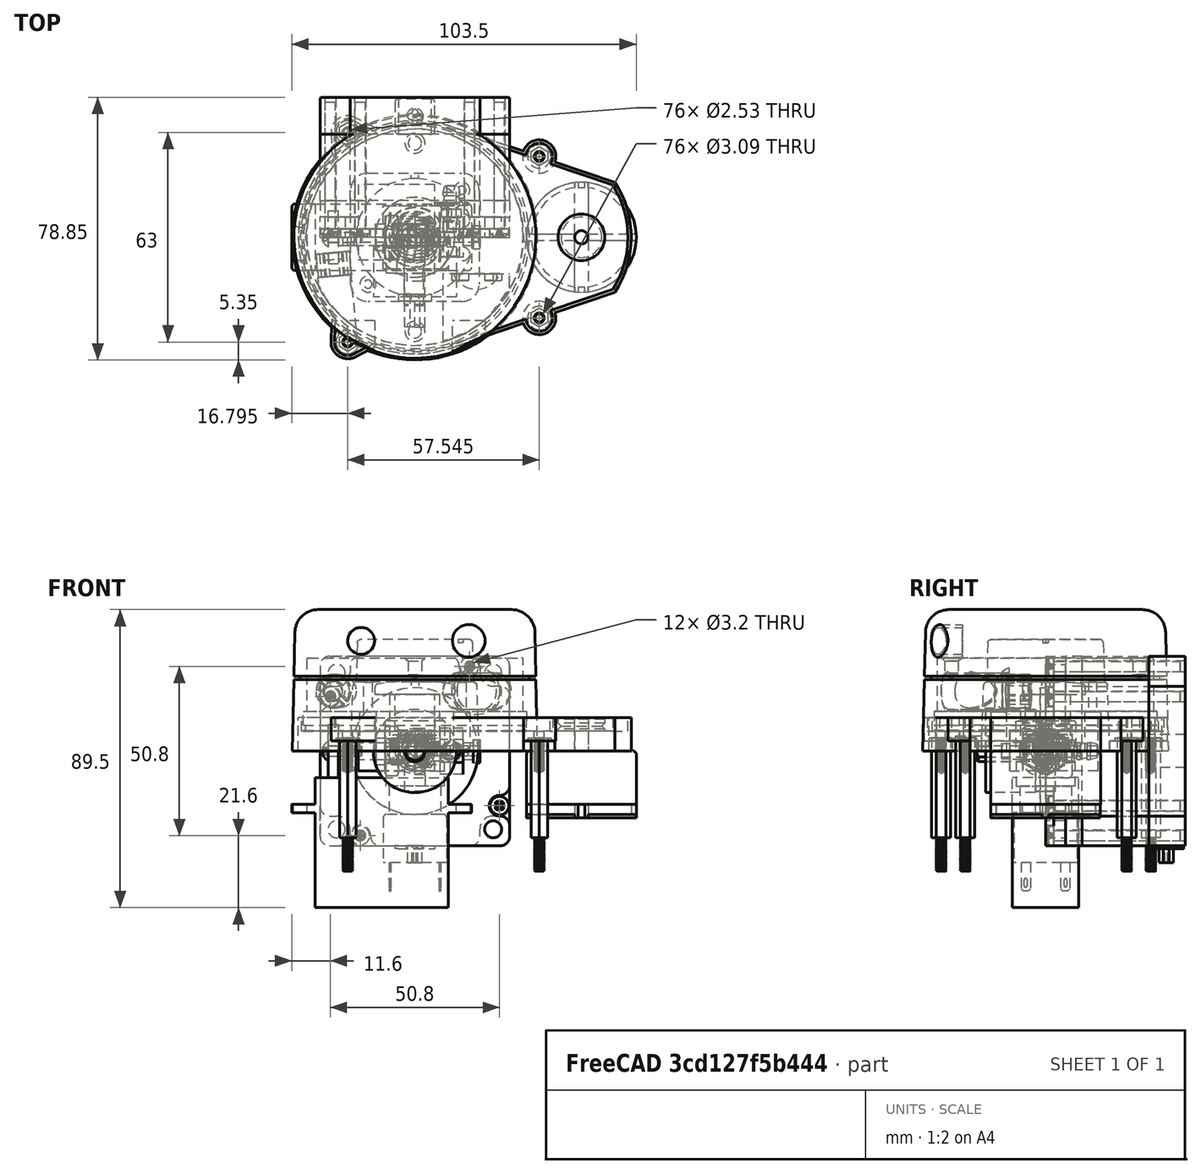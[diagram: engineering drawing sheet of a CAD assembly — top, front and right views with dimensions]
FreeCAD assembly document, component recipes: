
FREECAD ASSEMBLY — COMPONENT RECIPES ("generic-hardware")

This assembly document has 24 components, labeled P0..P23 below (a component is one placed body or linked part). 22 of them carry a construction recipe — the FreeCAD feature program that regenerates the part from scratch, quoted from this document or its linked companion documents; the rest are supplied as boundary geometry only. No exploded tour is included for this assembly.
NOTE — this tour is split across 2 documents so each fits a 32k-token context. This is document 1: the component sections continue in the remaining 1 document, each repeating the header above.
COMPONENT P0 — recipe-attached ("MKS_SERVO57B_", modeled in this document).
Construction recipe (the document's own serialized feature program — sketch geometry with constraints, then the solid features built on it; lengths are millimeters unless a unit is written):

FEATURE [Sketcher::SketchObject] Sketch
  ArcFitTolerance = 0
  AttachmentSupport = -> [XY_Plane]
  ExternalBSplineMaxDegree = 0
  ExternalBSplineTolerance = 0
  FixShape = 1
  FullyConstrained = true
  InternalTolerance = 1e-06
  InvalidShape = false
  MakeInternals = false
  MapMode = 5
  Support = -> [XY_Plane]
  TreeRank = 0
  ValidateShape = false
  sketch-geometry (8):
    g0: LineSegment StartX=-28 StartY=0 StartZ=0 EndX=-28 EndY=18.5 EndZ=0
    g1: LineSegment StartX=-28 StartY=18.5 StartZ=0 EndX=-18.5 EndY=18.5 EndZ=0
    g2: LineSegment StartX=-18.5 StartY=18.5 StartZ=0 EndX=-18.5 EndY=28 EndZ=0
    g3: LineSegment StartX=-18.5 StartY=28 StartZ=0 EndX=0 EndY=28 EndZ=0
    g4: LineSegment StartX=0 StartY=28 StartZ=0 EndX=0 EndY=0 EndZ=0
    g5: LineSegment StartX=0 StartY=0 StartZ=0 EndX=-28 EndY=0 EndZ=0
    g6: Circle CenterX=-16 CenterY=25.5 CenterZ=0 NormalX=0 NormalY=0 NormalZ=1 AngleXU=0 Radius=1.55
    g7: Circle CenterX=-25.5 CenterY=16 CenterZ=0 NormalX=0 NormalY=0 NormalZ=1 AngleXU=0 Radius=1.55
  constraints (23):
    c: PointOnObject(g0,g-1)
    c: Vertical(g0)
    c: Coincident(g0,g1)
    c: Coincident(g1,g2)
    c: Vertical(g2)
    c: Coincident(g2,g3)
    c: PointOnObject(g3,g-2)
    c: Horizontal(g3)
    c: Coincident(g3,g4)
    c: Coincident(g4,g-1)
    c: Coincident(g4,g5)
    c: Coincident(g5,g0)
    c: Horizontal(g1)
    c: Equal(g2,g1)
    c: DistanceX(g5,g5) = 28
    c: Equal(g4,g5)
    c: DistanceX(g1,g1) = 9.5
    c: Equal(g7,g6)
    c: Diameter(g6) = 3.1
    c: DistanceX(g6) = -16
    c: DistanceY(g6) = 25.5
    c: DistanceX(g7) = -25.5
    c: DistanceY(g7) = 16
FEATURE [PartDesign::Pad] Pad
  AddSubType = 0
  AutoTaperInnerAngle = false
  CheckUpToFaceLimits = true
  ClaimChildren = false
  Direction = (1,1,1)
  Fit = 0
  FitJoin = 0
  FixShape = 1
  InnerFit = 0
  InnerFitJoin = 0
  InvalidShape = false
  Length = 20
  Length2 = 100
  NewSolid = false
  Profile = -> Sketch
  Refine = true
  Suppress = false
  TaperInnerAngle = 0
  TaperInnerAngleRev = 0
  TreeRank = 0
  Type = 0
  ValidateShape = false
  _ProfileBasedVersion = 0
FEATURE [PartDesign::PolarPattern] PolarPattern012
  AddSubType = 0
  Angle = 360
  Axis = -> Sketch [N_Axis]
  BaseFeature = -> Pad
  CopyShape = false
  FixShape = 1
  InvalidShape = false
  NewSolid = false
  Occurrences = 4
  OriginalSubs = -> [Pad]
  Originals = -> [Pad]
  ParallelTransform = true
  Refine = true
  SubTransform = true
  Suppress = false
  TreeRank = 0
  ValidateShape = false
  _Version = 0
FEATURE [PartDesign::Fillet] Fillet004
  AddSubType = 0
  Base = -> PolarPattern012 [Edge2,Edge38,Edge11,Edge33]
  BaseFeature = -> PolarPattern012
  FixShape = 1
  InvalidShape = false
  NewSolid = false
  Radius = 4
  Refine = true
  SupportTransform = false
  Suppress = false
  TreeRank = 0
  UseAllEdges = false
  ValidateShape = false
FEATURE [PartDesign::Fillet] Fillet005
  AddSubType = 0
  Base = -> Fillet004 [Edge30,Edge58,Edge60,Edge63,Edge61,Edge55,Edge53,Edge3]
  BaseFeature = -> Fillet004
  FixShape = 1
  InvalidShape = false
  NewSolid = false
  Radius = 2.5
  Refine = true
  SupportTransform = false
  Suppress = false
  TreeRank = 0
  UseAllEdges = false
  ValidateShape = false
FEATURE [Sketcher::SketchObject] Sketch019
  ArcFitTolerance = 0
  AttachmentSupport = -> [XZ_Plane]
  ExternalBSplineMaxDegree = 0
  ExternalBSplineTolerance = 0
  FixShape = 1
  FullyConstrained = true
  InternalTolerance = 1e-06
  InvalidShape = false
  MakeInternals = false
  MapMode = 5
  Placement = pos=(0,0,0) rot=(1,0,0;1.5708rad)
  Support = -> [XZ_Plane]
  TreeRank = 0
  ValidateShape = false
  sketch-geometry (4):
    g0: LineSegment StartX=-7 StartY=10 StartZ=0 EndX=11 EndY=10 EndZ=0
    g1: LineSegment StartX=11 StartY=10 StartZ=0 EndX=11 EndY=3.5 EndZ=0
    g2: LineSegment StartX=11 StartY=3.5 StartZ=0 EndX=-7 EndY=3.5 EndZ=0
    g3: LineSegment StartX=-7 StartY=3.5 StartZ=0 EndX=-7 EndY=10 EndZ=0
  constraints (12):
    c: Coincident(g0,g1)
    c: Coincident(g1,g2)
    c: Coincident(g2,g3)
    c: Coincident(g3,g0)
    c: Horizontal(g0)
    c: Horizontal(g2)
    c: Vertical(g1)
    c: Vertical(g3)
    c: DistanceY(g1,g1) = 6.5
    c: DistanceX(g0,g0) = 18
    c: DistanceX(g0) = -7
    c: DistanceY(g0) = 10
FEATURE [PartDesign::Pad] Pad012
  AddSubType = 0
  AutoTaperInnerAngle = false
  BaseFeature = -> Fillet005
  CheckUpToFaceLimits = true
  ClaimChildren = false
  Direction = (1,1,1)
  Fit = 0
  FitJoin = 0
  FixShape = 1
  InnerFit = 0
  InnerFitJoin = 0
  InvalidShape = false
  Length = 31.5
  Length2 = 100
  NewSolid = false
  Profile = -> Sketch019
  Refine = true
  Suppress = false
  TaperInnerAngle = 0
  TaperInnerAngleRev = 0
  TreeRank = 0
  Type = 0
  ValidateShape = false
  _ProfileBasedVersion = 0
FEATURE [PartDesign::Body] Body  label="MKS_SERVO57B_"
  AutoGroupSolids = false
  ClaimAllChildren = false
  ExportMode = 0
  FixShape = 1
  Group = -> [Sketch,Pad,PolarPattern012,Fillet004,Fillet005,Sketch019,Pad012]
  InvalidShape = false
  Origin = -> Origin015
  SingleSolid = true
  Tip = -> Pad012
  TreeRank = 0
  ValidateShape = false
  _ExportChildren = -> [Pad,PolarPattern012,Fillet004,Fillet005,Pad012]
  _GroupVersion = 1
COMPONENT P1 — recipe-attached ("Corner", modeled in this document).
Construction recipe (the document's own serialized feature program — sketch geometry with constraints, then the solid features built on it; lengths are millimeters unless a unit is written):

FEATURE [Sketcher::SketchObject] Sketch001
  ArcFitTolerance = 0
  AttachmentSupport = -> [YZ_Plane001]
  ExternalBSplineMaxDegree = 0
  ExternalBSplineTolerance = 0
  FixShape = 1
  FullyConstrained = true
  InternalTolerance = 1e-06
  InvalidShape = false
  MakeInternals = false
  MapMode = 5
  Placement = pos=(0,0,0) rot=(0.57735,0.57735,0.57735;2.0944rad)
  Support = -> [YZ_Plane001]
  TreeRank = 0
  ValidateShape = false
  sketch-geometry (4):
    g0: LineSegment StartX=-5 StartY=5 StartZ=0 EndX=5 EndY=5 EndZ=0
    g1: LineSegment StartX=5 StartY=5 StartZ=0 EndX=5 EndY=-5 EndZ=0
    g2: LineSegment StartX=5 StartY=-5 StartZ=0 EndX=-5 EndY=-5 EndZ=0
    g3: LineSegment StartX=-5 StartY=-5 StartZ=0 EndX=-5 EndY=5 EndZ=0
  constraints (11):
    c: Coincident(g0,g1)
    c: Coincident(g1,g2)
    c: Coincident(g2,g3)
    c: Coincident(g3,g0)
    c: Horizontal(g0)
    c: Horizontal(g2)
    c: Vertical(g1)
    c: Vertical(g3)
    c: Symmetric(g1,g0,g-1)
    c: Equal(g0,g3)
    c: DistanceX(g0,g0) = 10
FEATURE [PartDesign::Pad] Pad001
  AddSubType = 0
  AutoTaperInnerAngle = false
  CheckUpToFaceLimits = true
  ClaimChildren = false
  Direction = (1,1,1)
  Fit = 0
  FitJoin = 0
  FixShape = 1
  InnerFit = 0
  InnerFitJoin = 0
  InvalidShape = false
  Length = 10
  Length2 = 100
  Midplane = true
  NewSolid = false
  Placement = pos=(0,0,0) rot=(0.57735,0.57735,0.57735;2.0944rad)
  Profile = -> Sketch001
  Refine = true
  Suppress = false
  TaperInnerAngle = 0
  TaperInnerAngleRev = 0
  TreeRank = 0
  Type = 0
  ValidateShape = false
  _ProfileBasedVersion = 0
FEATURE [Sketcher::SketchObject] Sketch002
  ArcFitTolerance = 0
  AttachmentSupport = -> [YZ_Plane001]
  ExternalBSplineMaxDegree = 0
  ExternalBSplineTolerance = 0
  FixShape = 1
  FullyConstrained = true
  InternalTolerance = 1e-06
  InvalidShape = false
  MakeInternals = false
  MapMode = 5
  Placement = pos=(0,0,0) rot=(0.57735,0.57735,0.57735;2.0944rad)
  Support = -> [YZ_Plane001]
  TreeRank = 0
  ValidateShape = false
  sketch-geometry (1):
    g0: Circle CenterX=0 CenterY=0 CenterZ=0 NormalX=0 NormalY=0 NormalZ=1 AngleXU=0 Radius=1.5
  constraints (2):
    c: Coincident(g0,g-1)
    c: Diameter(g0) = 3
FEATURE [PartDesign::Pocket] Pocket
  AddSubType = 1
  AutoTaperInnerAngle = false
  BaseFeature = -> Pad001
  CheckUpToFaceLimits = true
  ClaimChildren = false
  Direction = (1,1,1)
  Fit = 0
  FitJoin = 0
  FixShape = 1
  InnerFit = 0
  InnerFitJoin = 0
  InvalidShape = false
  Length = 5
  Length2 = 100
  Midplane = true
  NewSolid = false
  Placement = pos=(0,0,0) rot=(0.57735,0.57735,0.57735;2.0944rad)
  Profile = -> Sketch002
  Refine = true
  Suppress = false
  TaperInnerAngle = 0
  TaperInnerAngleRev = 0
  TreeRank = 0
  Type = 1
  ValidateShape = false
  _ProfileBasedVersion = 0
  _Version = 0
FEATURE [PartDesign::PolarPattern] PolarPattern
  AddSubType = 0
  Angle = 90
  Axis = -> Z_Axis001
  CopyShape = false
  FixShape = 1
  InvalidShape = false
  NewSolid = false
  Occurrences = 2
  ParallelTransform = true
  Placement = pos=(0,0,0) rot=(0.57735,0.57735,0.57735;2.0944rad)
  Refine = true
  SubTransform = true
  Suppress = false
  TreeRank = 0
  ValidateShape = false
  _Version = 0
FEATURE [PartDesign::PolarPattern] PolarPattern001
  AddSubType = 0
  Angle = 90
  Axis = -> Y_Axis001
  CopyShape = false
  FixShape = 1
  InvalidShape = false
  NewSolid = false
  Occurrences = 2
  ParallelTransform = true
  Placement = pos=(0,0,0) rot=(0.57735,0.57735,0.57735;2.0944rad)
  Refine = true
  SubTransform = true
  Suppress = false
  TreeRank = 0
  ValidateShape = false
  _Version = 0
FEATURE [PartDesign::MultiTransform] MultiTransform
  AddSubType = 0
  BaseFeature = -> Pocket
  CopyShape = false
  FixShape = 1
  InvalidShape = false
  NewSolid = false
  OriginalSubs = -> [Pocket]
  Originals = -> [Pocket]
  ParallelTransform = true
  Placement = pos=(0,0,0) rot=(0.57735,0.57735,0.57735;2.0944rad)
  Refine = true
  SubTransform = true
  Suppress = false
  Transformations = -> [PolarPattern,PolarPattern001]
  TreeRank = 0
  ValidateShape = false
  _Version = 0
FEATURE [PartDesign::Plane] DatumPlane
  AttachmentOffset = pos=(0,0,5) rot=(0,0,1;0rad)
  AttachmentSupport = -> [YZ_Plane001]
  FixShape = 1
  InvalidShape = false
  Length = 10
  MapMode = 5
  MinimumLength = 10
  MinimumWidth = 10
  Placement = pos=(5,-1.1e-15,1.1e-15) rot=(0.57735,0.57735,0.57735;2.0944rad)
  ResizeMode = 0
  Support = -> [YZ_Plane001]
  TreeRank = 0
  ValidateShape = false
  Width = 10
FEATURE [Sketcher::SketchObject] Sketch003
  ArcFitTolerance = 0
  AttachmentSupport = -> [DatumPlane]
  ExternalBSplineMaxDegree = 0
  ExternalBSplineTolerance = 0
  FixShape = 1
  FullyConstrained = true
  InternalTolerance = 1e-06
  InvalidShape = false
  MakeInternals = false
  MapMode = 5
  Placement = pos=(5,-1.1e-15,1.1e-15) rot=(0.57735,0.57735,0.57735;2.0944rad)
  Support = -> [DatumPlane]
  TreeRank = 0
  ValidateShape = false
  sketch-geometry (1):
    g0: Circle CenterX=0 CenterY=0 CenterZ=0 NormalX=0 NormalY=0 NormalZ=1 AngleXU=0 Radius=3
  constraints (2):
    c: Coincident(g0,g-1)
    c: Diameter(g0) = 6
FEATURE [PartDesign::Pocket] Pocket001
  AddSubType = 1
  AutoTaperInnerAngle = false
  BaseFeature = -> MultiTransform
  CheckUpToFaceLimits = true
  ClaimChildren = false
  Direction = (1,1,1)
  Fit = 0
  FitJoin = 0
  FixShape = 1
  InnerFit = 0
  InnerFitJoin = 0
  InvalidShape = false
  Length = 8
  Length2 = 100
  NewSolid = false
  Placement = pos=(0,0,0) rot=(0.57735,0.57735,0.57735;2.0944rad)
  Profile = -> Sketch003
  Refine = true
  Suppress = false
  TaperInnerAngle = 0
  TaperInnerAngleRev = 0
  TreeRank = 0
  Type = 0
  ValidateShape = false
  _ProfileBasedVersion = 0
  _Version = 0
FEATURE [PartDesign::PolarPattern] PolarPattern002
  AddSubType = 0
  Angle = 90
  Axis = -> Y_Axis001
  CopyShape = false
  FixShape = 1
  InvalidShape = false
  NewSolid = false
  Occurrences = 2
  ParallelTransform = true
  Placement = pos=(0,0,0) rot=(0.57735,0.57735,0.57735;2.0944rad)
  Refine = true
  SubTransform = true
  Suppress = false
  TreeRank = 0
  ValidateShape = false
  _Version = 0
FEATURE [PartDesign::PolarPattern] PolarPattern003
  AddSubType = 0
  Angle = 90
  Axis = -> Z_Axis001
  CopyShape = false
  FixShape = 1
  InvalidShape = false
  NewSolid = false
  Occurrences = 2
  ParallelTransform = true
  Placement = pos=(0,0,0) rot=(0.57735,0.57735,0.57735;2.0944rad)
  Refine = true
  SubTransform = true
  Suppress = false
  TreeRank = 0
  ValidateShape = false
  _Version = 0
FEATURE [PartDesign::MultiTransform] MultiTransform001
  AddSubType = 0
  BaseFeature = -> Pocket001
  CopyShape = false
  FixShape = 1
  InvalidShape = false
  NewSolid = false
  OriginalSubs = -> [Pocket001]
  Originals = -> [Pocket001]
  ParallelTransform = true
  Placement = pos=(0,0,0) rot=(0.57735,0.57735,0.57735;2.0944rad)
  Refine = true
  SubTransform = true
  Suppress = false
  Transformations = -> [PolarPattern002,PolarPattern003]
  TreeRank = 0
  ValidateShape = false
  _Version = 0
FEATURE [PartDesign::Body] Body001  label="Corner"
  AutoGroupSolids = false
  ClaimAllChildren = false
  ExportMode = 0
  FixShape = 1
  Group = -> [Sketch001,Pad001,Sketch002,Pocket,MultiTransform,PolarPattern,PolarPattern001,DatumPlane,Sketch003,Pocket001,MultiTransform001,PolarPattern002,PolarPattern003]
  InvalidShape = false
  Origin = -> Origin001
  SingleSolid = true
  Tip = -> MultiTransform001
  TreeRank = 0
  ValidateShape = false
  _ExportChildren = -> [Pad001,Pocket,MultiTransform,DatumPlane,Pocket001,MultiTransform001]
  _GroupVersion = 1
COMPONENT P2 — recipe-attached ("MB_100", modeled in this document).
Construction recipe (the document's own serialized feature program — sketch geometry with constraints, then the solid features built on it; lengths are millimeters unless a unit is written):

FEATURE [Sketcher::SketchObject] Sketch004
  ArcFitTolerance = 0
  AttachmentSupport = -> [XZ_Plane002]
  ExternalBSplineMaxDegree = 0
  ExternalBSplineTolerance = 0
  FixShape = 1
  FullyConstrained = true
  InternalTolerance = 1e-06
  InvalidShape = false
  MakeInternals = false
  MapMode = 5
  Placement = pos=(0,0,0) rot=(1,0,0;1.5708rad)
  Support = -> [XZ_Plane002]
  TreeRank = 0
  ValidateShape = false
  sketch-geometry (14):
    g0: ArcOfCircle CenterX=0 CenterY=0 CenterZ=0 NormalX=0 NormalY=0 NormalZ=1 AngleXU=0 Radius=1.25 StartAngle=0 EndAngle=1.5708
    g1: LineSegment StartX=1e-16 StartY=1.25 StartZ=0 EndX=0 EndY=2 EndZ=0
    g2: LineSegment StartX=0 StartY=2 StartZ=0 EndX=1 EndY=2 EndZ=0
    g3: LineSegment [constr] StartX=0 StartY=0 StartZ=0 EndX=5 EndY=5 EndZ=0
    g4: LineSegment StartX=1 StartY=2 StartZ=0 EndX=3.3 EndY=4 EndZ=0
    g5: LineSegment StartX=3.3 StartY=4 StartZ=0 EndX=1.5 EndY=4 EndZ=0
    g6: LineSegment StartX=1.5 StartY=4 StartZ=0 EndX=1.5 EndY=5 EndZ=0
    g7: LineSegment StartX=1.5 StartY=5 StartZ=0 EndX=5 EndY=5 EndZ=0
    g8: LineSegment StartX=5 StartY=5 StartZ=0 EndX=5 EndY=1.5 EndZ=0
    g9: LineSegment StartX=5 StartY=1.5 StartZ=0 EndX=4 EndY=1.5 EndZ=0
    g10: LineSegment StartX=4 StartY=1.5 StartZ=0 EndX=4 EndY=3.3 EndZ=0
    g11: LineSegment StartX=4 StartY=3.3 StartZ=0 EndX=2 EndY=1 EndZ=0
    g12: LineSegment StartX=2 StartY=1 StartZ=0 EndX=2 EndY=0 EndZ=0
    g13: LineSegment StartX=2 StartY=0 StartZ=0 EndX=1.25 EndY=0 EndZ=0
  constraints (41):
    c: Coincident(g0,g-1)
    c: PointOnObject(g0,g-1)
    c: PointOnObject(g0,g-2)
    c: Coincident(g1,g0)
    c: PointOnObject(g1,g-2)
    c: Coincident(g2,g1)
    c: Horizontal(g2)
    c: Coincident(g3,g0)
    c: Angle(g-1,g3) = 0.785398
    c: DistanceX(g3) = 5
    c: Diameter(g0) = 2.5
    c: DistanceX(g2) = 1
    c: Coincident(g4,g2)
    c: Coincident(g5,g4)
    c: Horizontal(g5)
    c: Coincident(g6,g5)
    c: Vertical(g6)
    c: Coincident(g7,g6)
    c: Coincident(g7,g3)
    c: Coincident(g8,g7)
    c: Vertical(g8)
    c: Coincident(g9,g8)
    c: Coincident(g10,g9)
    c: Vertical(g10)
    c: Coincident(g11,g10)
    c: Coincident(g12,g11)
    c: PointOnObject(g12,g-1)
    c: Vertical(g12)
    c: Coincident(g13,g12)
    c: Coincident(g13,g0)
    c: Equal(g12,g2)
    c: Equal(g13,g1)
    c: Horizontal(g7)
    c: Horizontal(g9)
    c: Equal(g6,g9)
    c: Equal(g11,g4)
    c: Equal(g5,g10)
    c: DistanceY(g2,g6) = 3
    c: DistanceX(g6) = 1.5
    c: DistanceY(g6,g6) = 1
    c: DistanceX(g5,g5) = 1.8
FEATURE [PartDesign::Pad] Pad002
  AddSubType = 0
  AutoTaperInnerAngle = false
  CheckUpToFaceLimits = true
  ClaimChildren = false
  Direction = (1,1,1)
  Fit = 0
  FitJoin = 0
  FixShape = 1
  InnerFit = 0
  InnerFitJoin = 0
  InvalidShape = false
  Length = 100
  Length2 = 100
  NewSolid = false
  Placement = pos=(0,0,0) rot=(1,0,0;1.5708rad)
  Profile = -> Sketch004
  Refine = true
  Reversed = true
  Suppress = false
  TaperInnerAngle = 0
  TaperInnerAngleRev = 0
  TreeRank = 0
  Type = 0
  ValidateShape = false
  _ProfileBasedVersion = 0
FEATURE [PartDesign::PolarPattern] PolarPattern004
  AddSubType = 0
  Angle = 360
  Axis = -> Y_Axis002
  BaseFeature = -> Pad002
  CopyShape = false
  FixShape = 1
  InvalidShape = false
  NewSolid = false
  Occurrences = 4
  OriginalSubs = -> [Pad002]
  Originals = -> [Pad002]
  ParallelTransform = true
  Placement = pos=(0,0,0) rot=(1,0,0;1.5708rad)
  Refine = true
  SubTransform = true
  Suppress = false
  TreeRank = 0
  ValidateShape = false
  _Version = 0
FEATURE [PartDesign::CoordinateSystem] Local_CS
  AttacherType = Attacher::AttachEngine3D
  AttachmentSupport = -> [PolarPattern004]
  FixShape = 1
  InvalidShape = false
  Placement = pos=(4.44e-14,100,0) rot=(1,0,0;1.5708rad)
  Support = -> [PolarPattern004]
  TreeRank = 0
  ValidateShape = false
FEATURE [PartDesign::Body] Body002  label="MB_100"
  AutoGroupSolids = false
  ClaimAllChildren = false
  ExportMode = 0
  FixShape = 1
  Group = -> [Sketch004,Pad002,PolarPattern004,Local_CS]
  InvalidShape = false
  Origin = -> Origin002
  SingleSolid = true
  Tip = -> PolarPattern004
  TreeRank = 0
  ValidateShape = false
  _ExportChildren = -> [Pad002,PolarPattern004,Local_CS]
  _GroupVersion = 1
COMPONENT P3 — recipe-attached ("MB_60", modeled in this document).
Construction recipe (the document's own serialized feature program — sketch geometry with constraints, then the solid features built on it; lengths are millimeters unless a unit is written):

FEATURE [Sketcher::SketchObject] Sketch005
  ArcFitTolerance = 0
  AttachmentSupport = -> [XZ_Plane003]
  ExternalBSplineMaxDegree = 0
  ExternalBSplineTolerance = 0
  FixShape = 1
  FullyConstrained = true
  InternalTolerance = 1e-06
  InvalidShape = false
  MakeInternals = false
  MapMode = 5
  Placement = pos=(0,0,0) rot=(1,0,0;1.5708rad)
  Support = -> [XZ_Plane003]
  TreeRank = 0
  ValidateShape = false
  sketch-geometry (14):
    g0: ArcOfCircle CenterX=0 CenterY=0 CenterZ=0 NormalX=0 NormalY=0 NormalZ=1 AngleXU=0 Radius=1.25 StartAngle=0 EndAngle=1.5708
    g1: LineSegment StartX=1e-16 StartY=1.25 StartZ=0 EndX=0 EndY=2 EndZ=0
    g2: LineSegment StartX=0 StartY=2 StartZ=0 EndX=1 EndY=2 EndZ=0
    g3: LineSegment [constr] StartX=0 StartY=0 StartZ=0 EndX=5 EndY=5 EndZ=0
    g4: LineSegment StartX=1 StartY=2 StartZ=0 EndX=3.3 EndY=4 EndZ=0
    g5: LineSegment StartX=3.3 StartY=4 StartZ=0 EndX=1.5 EndY=4 EndZ=0
    g6: LineSegment StartX=1.5 StartY=4 StartZ=0 EndX=1.5 EndY=5 EndZ=0
    g7: LineSegment StartX=1.5 StartY=5 StartZ=0 EndX=5 EndY=5 EndZ=0
    g8: LineSegment StartX=5 StartY=5 StartZ=0 EndX=5 EndY=1.5 EndZ=0
    g9: LineSegment StartX=5 StartY=1.5 StartZ=0 EndX=4 EndY=1.5 EndZ=0
    g10: LineSegment StartX=4 StartY=1.5 StartZ=0 EndX=4 EndY=3.3 EndZ=0
    g11: LineSegment StartX=4 StartY=3.3 StartZ=0 EndX=2 EndY=1 EndZ=0
    g12: LineSegment StartX=2 StartY=1 StartZ=0 EndX=2 EndY=0 EndZ=0
    g13: LineSegment StartX=2 StartY=0 StartZ=0 EndX=1.25 EndY=0 EndZ=0
  constraints (41):
    c: Coincident(g0,g-1)
    c: PointOnObject(g0,g-1)
    c: PointOnObject(g0,g-2)
    c: Coincident(g1,g0)
    c: PointOnObject(g1,g-2)
    c: Coincident(g2,g1)
    c: Horizontal(g2)
    c: Coincident(g3,g0)
    c: Angle(g-1,g3) = 0.785398
    c: DistanceX(g3) = 5
    c: Diameter(g0) = 2.5
    c: DistanceX(g2) = 1
    c: Coincident(g4,g2)
    c: Coincident(g5,g4)
    c: Horizontal(g5)
    c: Coincident(g6,g5)
    c: Vertical(g6)
    c: Coincident(g7,g6)
    c: Coincident(g7,g3)
    c: Coincident(g8,g7)
    c: Vertical(g8)
    c: Coincident(g9,g8)
    c: Coincident(g10,g9)
    c: Vertical(g10)
    c: Coincident(g11,g10)
    c: Coincident(g12,g11)
    c: PointOnObject(g12,g-1)
    c: Vertical(g12)
    c: Coincident(g13,g12)
    c: Coincident(g13,g0)
    c: Equal(g12,g2)
    c: Equal(g13,g1)
    c: Horizontal(g7)
    c: Horizontal(g9)
    c: Equal(g6,g9)
    c: Equal(g11,g4)
    c: Equal(g5,g10)
    c: DistanceY(g2,g6) = 3
    c: DistanceX(g6) = 1.5
    c: DistanceY(g6,g6) = 1
    c: DistanceX(g5,g5) = 1.8
FEATURE [PartDesign::Pad] Pad003
  AddSubType = 0
  AutoTaperInnerAngle = false
  CheckUpToFaceLimits = true
  ClaimChildren = false
  Direction = (1,1,1)
  Fit = 0
  FitJoin = 0
  FixShape = 1
  InnerFit = 0
  InnerFitJoin = 0
  InvalidShape = false
  Length = 60
  Length2 = 100
  NewSolid = false
  Placement = pos=(0,0,0) rot=(1,0,0;1.5708rad)
  Profile = -> Sketch005
  Refine = true
  Reversed = true
  Suppress = false
  TaperInnerAngle = 0
  TaperInnerAngleRev = 0
  TreeRank = 0
  Type = 0
  ValidateShape = false
  _ProfileBasedVersion = 0
FEATURE [PartDesign::PolarPattern] PolarPattern005
  AddSubType = 0
  Angle = 360
  AttacherType = Attacher::AttachEngine3D
  Axis = -> Y_Axis003
  BaseFeature = -> Pad003
  CopyShape = false
  FixShape = 1
  InvalidShape = false
  NewSolid = false
  Occurrences = 4
  OriginalSubs = -> [Pad003]
  Originals = -> [Pad003]
  ParallelTransform = true
  Placement = pos=(0,0,0) rot=(1,0,0;1.5708rad)
  Refine = true
  SubTransform = true
  Suppress = false
  TreeRank = 0
  ValidateShape = false
  _Version = 0
FEATURE [PartDesign::CoordinateSystem] Local_CS001
  AttacherType = Attacher::AttachEngine3D
  AttachmentSupport = -> [PolarPattern005]
  FixShape = 1
  InvalidShape = false
  MapMode = 11
  Placement = pos=(2.66e-14,60,-1.33e-14) rot=(1,0,0;1.5708rad)
  Support = -> [PolarPattern005]
  TreeRank = 0
  ValidateShape = false
FEATURE [PartDesign::Body] Body003  label="MB_60"
  AutoGroupSolids = false
  ClaimAllChildren = false
  ExportMode = 0
  FixShape = 1
  Group = -> [Sketch005,Pad003,PolarPattern005,Local_CS001]
  InvalidShape = false
  Origin = -> Origin003
  SingleSolid = true
  Tip = -> PolarPattern005
  TreeRank = 0
  ValidateShape = false
  _ExportChildren = -> [Pad003,PolarPattern005,Local_CS001]
  _GroupVersion = 1
COMPONENT P4 — recipe-attached ("MB_300", modeled in this document).
Construction recipe (the document's own serialized feature program — sketch geometry with constraints, then the solid features built on it; lengths are millimeters unless a unit is written):

FEATURE [Sketcher::SketchObject] Sketch006
  ArcFitTolerance = 0
  AttachmentSupport = -> [XZ_Plane004]
  ExternalBSplineMaxDegree = 0
  ExternalBSplineTolerance = 0
  FixShape = 1
  FullyConstrained = true
  InternalTolerance = 1e-06
  InvalidShape = false
  MakeInternals = false
  MapMode = 5
  Placement = pos=(0,0,0) rot=(1,0,0;1.5708rad)
  Support = -> [XZ_Plane004]
  TreeRank = 0
  ValidateShape = false
  sketch-geometry (14):
    g0: ArcOfCircle CenterX=0 CenterY=0 CenterZ=0 NormalX=0 NormalY=0 NormalZ=1 AngleXU=0 Radius=1.25 StartAngle=0 EndAngle=1.5708
    g1: LineSegment StartX=1e-16 StartY=1.25 StartZ=0 EndX=0 EndY=2 EndZ=0
    g2: LineSegment StartX=0 StartY=2 StartZ=0 EndX=1 EndY=2 EndZ=0
    g3: LineSegment [constr] StartX=0 StartY=0 StartZ=0 EndX=5 EndY=5 EndZ=0
    g4: LineSegment StartX=1 StartY=2 StartZ=0 EndX=3.3 EndY=4 EndZ=0
    g5: LineSegment StartX=3.3 StartY=4 StartZ=0 EndX=1.5 EndY=4 EndZ=0
    g6: LineSegment StartX=1.5 StartY=4 StartZ=0 EndX=1.5 EndY=5 EndZ=0
    g7: LineSegment StartX=1.5 StartY=5 StartZ=0 EndX=5 EndY=5 EndZ=0
    g8: LineSegment StartX=5 StartY=5 StartZ=0 EndX=5 EndY=1.5 EndZ=0
    g9: LineSegment StartX=5 StartY=1.5 StartZ=0 EndX=4 EndY=1.5 EndZ=0
    g10: LineSegment StartX=4 StartY=1.5 StartZ=0 EndX=4 EndY=3.3 EndZ=0
    g11: LineSegment StartX=4 StartY=3.3 StartZ=0 EndX=2 EndY=1 EndZ=0
    g12: LineSegment StartX=2 StartY=1 StartZ=0 EndX=2 EndY=0 EndZ=0
    g13: LineSegment StartX=2 StartY=0 StartZ=0 EndX=1.25 EndY=0 EndZ=0
  constraints (41):
    c: Coincident(g0,g-1)
    c: PointOnObject(g0,g-1)
    c: PointOnObject(g0,g-2)
    c: Coincident(g1,g0)
    c: PointOnObject(g1,g-2)
    c: Coincident(g2,g1)
    c: Horizontal(g2)
    c: Coincident(g3,g0)
    c: Angle(g-1,g3) = 0.785398
    c: DistanceX(g3) = 5
    c: Diameter(g0) = 2.5
    c: DistanceX(g2) = 1
    c: Coincident(g4,g2)
    c: Coincident(g5,g4)
    c: Horizontal(g5)
    c: Coincident(g6,g5)
    c: Vertical(g6)
    c: Coincident(g7,g6)
    c: Coincident(g7,g3)
    c: Coincident(g8,g7)
    c: Vertical(g8)
    c: Coincident(g9,g8)
    c: Coincident(g10,g9)
    c: Vertical(g10)
    c: Coincident(g11,g10)
    c: Coincident(g12,g11)
    c: PointOnObject(g12,g-1)
    c: Vertical(g12)
    c: Coincident(g13,g12)
    c: Coincident(g13,g0)
    c: Equal(g12,g2)
    c: Equal(g13,g1)
    c: Horizontal(g7)
    c: Horizontal(g9)
    c: Equal(g6,g9)
    c: Equal(g11,g4)
    c: Equal(g5,g10)
    c: DistanceY(g2,g6) = 3
    c: DistanceX(g6) = 1.5
    c: DistanceY(g6,g6) = 1
    c: DistanceX(g5,g5) = 1.8
FEATURE [PartDesign::Pad] Pad004
  AddSubType = 0
  AutoTaperInnerAngle = false
  CheckUpToFaceLimits = true
  ClaimChildren = false
  Direction = (1,1,1)
  Fit = 0
  FitJoin = 0
  FixShape = 1
  InnerFit = 0
  InnerFitJoin = 0
  InvalidShape = false
  Length = 300
  Length2 = 100
  NewSolid = false
  Placement = pos=(0,0,0) rot=(1,0,0;1.5708rad)
  Profile = -> Sketch006
  Refine = true
  Reversed = true
  Suppress = false
  TaperInnerAngle = 0
  TaperInnerAngleRev = 0
  TreeRank = 0
  Type = 0
  ValidateShape = false
  _ProfileBasedVersion = 0
FEATURE [PartDesign::PolarPattern] PolarPattern006
  AddSubType = 0
  Angle = 360
  Axis = -> Y_Axis004
  BaseFeature = -> Pad004
  CopyShape = false
  FixShape = 1
  InvalidShape = false
  NewSolid = false
  Occurrences = 4
  OriginalSubs = -> [Pad004]
  Originals = -> [Pad004]
  ParallelTransform = true
  Placement = pos=(0,0,0) rot=(1,0,0;1.5708rad)
  Refine = true
  SubTransform = true
  Suppress = false
  TreeRank = 0
  ValidateShape = false
  _Version = 0
FEATURE [PartDesign::CoordinateSystem] Local_CS002
  AttacherType = Attacher::AttachEngine3D
  AttachmentSupport = -> [PolarPattern006]
  FixShape = 1
  InvalidShape = false
  MapMode = 11
  Placement = pos=(1.332e-13,300,-6.66e-14) rot=(1,0,0;1.5708rad)
  Support = -> [PolarPattern006]
  TreeRank = 0
  ValidateShape = false
FEATURE [PartDesign::Body] Body004  label="MB_300"
  AutoGroupSolids = false
  ClaimAllChildren = false
  ExportMode = 0
  FixShape = 1
  Group = -> [Sketch006,Pad004,PolarPattern006,Local_CS002]
  InvalidShape = false
  Origin = -> Origin004
  SingleSolid = true
  Tip = -> PolarPattern006
  TreeRank = 0
  ValidateShape = false
  _ExportChildren = -> [Pad004,PolarPattern006,Local_CS002]
  _GroupVersion = 1
COMPONENT P5 — recipe-attached ("ServoPalonnier", modeled in this document).
Construction recipe (the document's own serialized feature program — sketch geometry with constraints, then the solid features built on it; lengths are millimeters unless a unit is written):

FEATURE [Sketcher::SketchObject] Sketch088
  ArcFitTolerance = 0
  AttachmentSupport = -> [XY_Plane050]
  ExternalBSplineMaxDegree = 0
  ExternalBSplineTolerance = 0
  FixShape = 1
  FullyConstrained = true
  InternalTolerance = 1e-06
  InvalidShape = false
  MakeInternals = false
  MapMode = 5
  Support = -> [XY_Plane050]
  TreeRank = 0
  ValidateShape = false
  sketch-geometry (7):
    g0: Circle CenterX=0 CenterY=0 CenterZ=0 NormalX=0 NormalY=0 NormalZ=1 AngleXU=0 Radius=10
    g1: Circle CenterX=0 CenterY=7 CenterZ=0 NormalX=0 NormalY=0 NormalZ=1 AngleXU=0 Radius=1.5
    g2: Circle CenterX=7 CenterY=0 CenterZ=0 NormalX=0 NormalY=0 NormalZ=1 AngleXU=0 Radius=1.5
    g3: Circle CenterX=0 CenterY=-7 CenterZ=0 NormalX=0 NormalY=0 NormalZ=1 AngleXU=0 Radius=1.5
    g4: Circle CenterX=-7 CenterY=0 CenterZ=0 NormalX=0 NormalY=0 NormalZ=1 AngleXU=0 Radius=1.5
    g5: Circle [constr] CenterX=0 CenterY=0 CenterZ=0 NormalX=0 NormalY=0 NormalZ=1 AngleXU=0 Radius=7
    g6: Circle CenterX=0 CenterY=0 CenterZ=0 NormalX=0 NormalY=0 NormalZ=1 AngleXU=0 Radius=1.5
  constraints (18):
    c: Coincident(g0,g-1)
    c: Diameter(g0) = 20
    c: PointOnObject(g1,g-2)
    c: PointOnObject(g2,g-1)
    c: PointOnObject(g3,g-2)
    c: PointOnObject(g4,g-1)
    c: Equal(g4,g1)
    c: Equal(g1,g2)
    c: Equal(g2,g3)
    c: Diameter(g1) = 3
    c: Coincident(g5,g0)
    c: PointOnObject(g1,g5)
    c: PointOnObject(g2,g5)
    c: PointOnObject(g3,g5)
    c: PointOnObject(g4,g5)
    c: DistanceX(g4,g2) = 14
    c: Coincident(g6,g0)
    c: Equal(g2,g6)
FEATURE [PartDesign::Pad] Pad052
  AddSubType = 0
  AutoTaperInnerAngle = false
  CheckUpToFaceLimits = true
  ClaimChildren = false
  Direction = (1,1,1)
  Fit = 0
  FitJoin = 0
  FixShape = 1
  InnerFit = 0
  InnerFitJoin = 0
  InvalidShape = false
  Length = 2
  Length2 = 100
  Linearize = true
  NewSolid = false
  Profile = -> Sketch088
  Refine = true
  Reversed = true
  Suppress = false
  TaperInnerAngle = 0
  TaperInnerAngleRev = 0
  TreeRank = 0
  Type = 0
  ValidateShape = false
  _ProfileBasedVersion = 1
FEATURE [Sketcher::SketchObject] Sketch089
  ArcFitTolerance = 0
  AttachmentSupport = -> [XY_Plane050]
  ExternalBSplineMaxDegree = 0
  ExternalBSplineTolerance = 0
  FixShape = 1
  FullyConstrained = true
  InternalTolerance = 1e-06
  InvalidShape = false
  MakeInternals = false
  MapMode = 5
  Support = -> [XY_Plane050]
  TreeRank = 0
  ValidateShape = false
  sketch-geometry (2):
    g0: Circle CenterX=0 CenterY=0 CenterZ=0 NormalX=0 NormalY=0 NormalZ=1 AngleXU=0 Radius=4.7
    g1: Circle CenterX=0 CenterY=0 CenterZ=0 NormalX=0 NormalY=0 NormalZ=1 AngleXU=0 Radius=3
  constraints (4):
    c: Coincident(g0,g-1)
    c: Coincident(g1,g0)
    c: Diameter(g0) = 9.4
    c: Diameter(g1) = 6
FEATURE [PartDesign::Pad] Pad051
  AddSubType = 0
  AutoTaperInnerAngle = false
  BaseFeature = -> Pad052
  CheckUpToFaceLimits = true
  ClaimChildren = false
  Direction = (1,1,1)
  Fit = 0
  FitJoin = 0
  FixShape = 1
  InnerFit = 0
  InnerFitJoin = 0
  InvalidShape = false
  Length = 5.4
  Length2 = 100
  Linearize = true
  NewSolid = false
  Profile = -> Sketch089
  Refine = true
  Reversed = true
  Suppress = false
  TaperInnerAngle = 0
  TaperInnerAngleRev = 0
  TreeRank = 0
  Type = 0
  ValidateShape = false
  _ProfileBasedVersion = 1
FEATURE [PartDesign::Body] Body042  label="ServoPalonnier"
  AutoGroupSolids = false
  ClaimAllChildren = false
  ExportMode = 0
  FixShape = 1
  Group = -> [Sketch088,Pad052,Sketch089,Pad051]
  InvalidShape = false
  Origin = -> Origin063
  Placement = pos=(0,0,0) rot=(1,0,0;1.5708rad)
  SingleSolid = true
  Tip = -> Pad051
  TreeRank = 0
  ValidateShape = false
  _ExportChildren = -> [Pad052,Pad051]
  _GroupVersion = 1
COMPONENT P6 — recipe-attached ("PalonnierElastique", modeled in this document).
Construction recipe (the document's own serialized feature program — sketch geometry with constraints, then the solid features built on it; lengths are millimeters unless a unit is written):

FEATURE [Sketcher::SketchObject] Sketch123
  ArcFitTolerance = 0
  AttachmentSupport = -> [XZ_Plane068]
  ExternalBSplineMaxDegree = 0
  ExternalBSplineTolerance = 0
  FixShape = 1
  FullyConstrained = false
  InternalTolerance = 1e-06
  InvalidShape = false
  MakeInternals = false
  MapMode = 5
  Placement = pos=(0,0,0) rot=(1,0,0;1.5708rad)
  Support = -> [XZ_Plane068]
  TreeRank = 0
  ValidateShape = false
  sketch-geometry (17):
    g0: ArcOfCircle CenterX=0 CenterY=0 CenterZ=0 NormalX=0 NormalY=0 NormalZ=1 AngleXU=0 Radius=8 StartAngle=5.67415 EndAngle=10.0338
    g1: ArcOfCircle CenterX=-2e-15 CenterY=1 CenterZ=0 NormalX=0 NormalY=0 NormalZ=1 AngleXU=0 Radius=26 StartAngle=4.4405 EndAngle=4.98428
    g2: ArcOfCircle CenterX=6.42512 CenterY=-22.0462 CenterZ=0 NormalX=0 NormalY=0 NormalZ=1 AngleXU=0 Radius=2.07488 StartAngle=4.98428 EndAngle=6.60035
    g3: ArcOfCircle CenterX=-6.42512 CenterY=-22.0462 CenterZ=0 NormalX=0 NormalY=0 NormalZ=1 AngleXU=0 Radius=2.07488 StartAngle=2.82442 EndAngle=4.4405
    g4: LineSegment [constr] StartX=8.5 StartY=0 StartZ=0 EndX=8.5 EndY=-36.4357 EndZ=0
    g5: GeomPoint [constr] X=0 Y=-25 Z=0
    g6: GeomPoint [constr] X=0 Y=8 Z=0
    g7: Circle CenterX=-5.5 CenterY=-21 CenterZ=0 NormalX=0 NormalY=0 NormalZ=1 AngleXU=0 Radius=1.5
    g8: Circle CenterX=0 CenterY=-21 CenterZ=0 NormalX=0 NormalY=0 NormalZ=1 AngleXU=0 Radius=1.5
    g9: Circle CenterX=5.5 CenterY=-21 CenterZ=0 NormalX=0 NormalY=0 NormalZ=1 AngleXU=0 Radius=1.5
    g10: Circle CenterX=-4 CenterY=-17 CenterZ=0 NormalX=0 NormalY=0 NormalZ=1 AngleXU=0 Radius=1.5
    g11: Circle CenterX=4 CenterY=-17 CenterZ=0 NormalX=0 NormalY=0 NormalZ=1 AngleXU=0 Radius=1.5
    g12: LineSegment StartX=8.39651 StartY=-21.3991 StartZ=0 EndX=5.42128 EndY=-12.3352 EndZ=0
    g13: LineSegment StartX=-8.39651 StartY=-21.3991 StartZ=0 EndX=-5.42128 EndY=-12.3352 EndZ=0
    g14: ArcOfCircle CenterX=-13.7607 CenterY=-9.59779 CenterZ=0 NormalX=0 NormalY=0 NormalZ=1 AngleXU=0 Radius=8.77717 StartAngle=5.96602 EndAngle=6.89222
    g15: ArcOfCircle CenterX=13.7607 CenterY=-9.59779 CenterZ=0 NormalX=0 NormalY=0 NormalZ=1 AngleXU=0 Radius=8.77717 StartAngle=2.53256 EndAngle=3.45876
    g16: LineSegment [constr] StartX=-5 StartY=-9.05974 StartZ=0 EndX=5 EndY=-9.05974 EndZ=0
  constraints (42):
    c: Coincident(g0,g-1)
    c: Diameter(g0) = 16
    c: Symmetric(g1,g1,g-2)
    c: Symmetric(g0,g0,g-2)
    c: Tangent(g3,g1) = -1.5708
    c: Tangent(g2,g1) = -1.5708
    c: Symmetric(g3,g2,g-2)
    c: PointOnObject(g4,g-1)
    c: Vertical(g4)
    c: Tangent(g2,g4)
    c: DistanceX(g4) = 8.5
    c: PointOnObject(g5,g1)
    c: PointOnObject(g6,g0)
    c: PointOnObject(g6,g-2)
    c: PointOnObject(g5,g-2)
    c: DistanceY(g5,g6) = 33
    c: PointOnObject(g8,g-2)
    c: Horizontal(g7,g8)
    c: Symmetric(g10,g11,g-2)
    c: Symmetric(g7,g9,g-2)
    c: DistanceY(g11) = -17
    c: DistanceY(g9) = -21
    c: Diameter(g7) = 3
    c: Equal(g7,g10)
    c: Equal(g7,g8)
    c: Equal(g7,g9)
    c: Equal(g7,g11)
    c: DistanceX(g7,g9) = 11
    c: DistanceX(g10,g11) = 8
    c: Tangent(g13,g3) = 1.5708
    c: Tangent(g12,g2) = -1.5708
    c: Symmetric(g12,g13,g-2)
    c: Tangent(g15,g12) = 1.5708
    c: Tangent(g15,g0) = 1.5708
    c: PointOnObject(g16,g14)
    c: Horizontal(g16)
    c: PointOnObject(g16,g15)
    c: DistanceX(g16,g16) = 10
    c: Tangent(g14,g13) = -1.5708
    c: Tangent(g14,g0) = 1.5708
    c: Distance(g2,g1) = 3
    c: Diameter(g1) = 52
FEATURE [PartDesign::Pad] Pad066
  AddSubType = 0
  AutoTaperInnerAngle = false
  CheckUpToFaceLimits = true
  ClaimChildren = false
  Direction = (1,1,1)
  Fit = 0
  FitJoin = 0
  FixShape = 1
  InnerFit = 0
  InnerFitJoin = 0
  InvalidShape = false
  Length = 4
  Length2 = 100
  Linearize = true
  NewSolid = false
  Placement = pos=(0,0,0) rot=(1,0,0;1.5708rad)
  Profile = -> Sketch123
  Refine = true
  Reversed = true
  Suppress = false
  TaperInnerAngle = 0
  TaperInnerAngleRev = 0
  TreeRank = 0
  Type = 0
  ValidateShape = false
  _ProfileBasedVersion = 1
FEATURE [Sketcher::SketchObject] Sketch124
  ArcFitTolerance = 0
  AttachmentSupport = -> [XZ_Plane068]
  ExternalBSplineMaxDegree = 0
  ExternalBSplineTolerance = 0
  FixShape = 1
  FullyConstrained = true
  InternalTolerance = 1e-06
  InvalidShape = false
  MakeInternals = false
  MapMode = 5
  Placement = pos=(0,0,0) rot=(1,0,0;1.5708rad)
  Support = -> [XZ_Plane068]
  TreeRank = 0
  ValidateShape = false
  sketch-geometry (1):
    g0: Circle CenterX=0 CenterY=0 CenterZ=0 NormalX=0 NormalY=0 NormalZ=1 AngleXU=0 Radius=8
  constraints (2):
    c: Coincident(g0,g-1)
    c: Diameter(g0) = 16
FEATURE [PartDesign::Pad] Pad067
  AddSubType = 0
  AutoTaperInnerAngle = false
  BaseFeature = -> Pad066
  CheckUpToFaceLimits = true
  ClaimChildren = false
  Direction = (1,1,1)
  Fit = 0
  FitJoin = 0
  FixShape = 1
  InnerFit = 0
  InnerFitJoin = 0
  InvalidShape = false
  Length = 10
  Length2 = 100
  Linearize = true
  NewSolid = false
  Placement = pos=(0,0,0) rot=(1,0,0;1.5708rad)
  Profile = -> Sketch124
  Refine = true
  Reversed = true
  Suppress = false
  TaperInnerAngle = 0
  TaperInnerAngleRev = 0
  TreeRank = 0
  Type = 0
  ValidateShape = false
  _ProfileBasedVersion = 1
FEATURE [Sketcher::SketchObject] Sketch125
  ArcFitTolerance = 0
  AttachmentSupport = -> [Pad067]
  ExternalBSplineMaxDegree = 0
  ExternalBSplineTolerance = 0
  FixShape = 1
  FullyConstrained = true
  InternalTolerance = 1e-06
  InvalidShape = false
  MakeInternals = false
  MapMode = 5
  Placement = pos=(0,10,2.2e-15) rot=(-1,0,0;1.5708rad)
  Support = -> [Pad067]
  TreeRank = 0
  ValidateShape = false
  sketch-geometry (1):
    g0: Circle CenterX=0 CenterY=0 CenterZ=0 NormalX=0 NormalY=0 NormalZ=1 AngleXU=0 Radius=3
  constraints (2):
    c: Coincident(g0,g-1)
    c: Diameter(g0) = 6
FEATURE [PartDesign::Pocket] Pocket049
  AddSubType = 1
  AutoTaperInnerAngle = false
  BaseFeature = -> Pad067
  CheckUpToFaceLimits = true
  ClaimChildren = false
  Direction = (1,1,1)
  Fit = 0
  FitJoin = 0
  FixShape = 1
  InnerFit = 0
  InnerFitJoin = 0
  InvalidShape = false
  Length = 3.2
  Length2 = 100
  Linearize = true
  NewSolid = false
  Placement = pos=(0,0,0) rot=(1,0,0;1.5708rad)
  Profile = -> Sketch125
  Refine = true
  Suppress = false
  TaperInnerAngle = 0
  TaperInnerAngleRev = 0
  TreeRank = 0
  Type = 0
  ValidateShape = false
  _ProfileBasedVersion = 1
  _Version = 1
FEATURE [Sketcher::SketchObject] Sketch126
  ArcFitTolerance = 0
  AttachmentSupport = -> [XZ_Plane068]
  ExternalBSplineMaxDegree = 0
  ExternalBSplineTolerance = 0
  FixShape = 1
  FullyConstrained = true
  InternalTolerance = 1e-06
  InvalidShape = false
  MakeInternals = false
  MapMode = 5
  Placement = pos=(0,0,0) rot=(1,0,0;1.5708rad)
  Support = -> [XZ_Plane068]
  TreeRank = 0
  ValidateShape = false
  sketch-geometry (1):
    g0: Circle CenterX=0 CenterY=0 CenterZ=0 NormalX=0 NormalY=0 NormalZ=1 AngleXU=0 Radius=1.5
  constraints (2):
    c: Coincident(g0,g-1)
    c: Diameter(g0) = 3
FEATURE [PartDesign::Pocket] Pocket050
  AddSubType = 1
  AutoTaperInnerAngle = false
  BaseFeature = -> Pocket049
  CheckUpToFaceLimits = true
  ClaimChildren = false
  Direction = (1,1,1)
  Fit = 0
  FitJoin = 0
  FixShape = 1
  InnerFit = 0
  InnerFitJoin = 0
  InvalidShape = false
  Length = 5
  Length2 = 100
  Linearize = true
  NewSolid = false
  Placement = pos=(0,0,0) rot=(1,0,0;1.5708rad)
  Profile = -> Sketch126
  Refine = true
  Suppress = false
  TaperInnerAngle = 0
  TaperInnerAngleRev = 0
  TreeRank = 0
  Type = 1
  ValidateShape = false
  _ProfileBasedVersion = 1
  _Version = 1
FEATURE [Sketcher::SketchObject] Sketch127
  ArcFitTolerance = 0
  AttachmentSupport = -> [XZ_Plane068]
  ExternalBSplineMaxDegree = 0
  ExternalBSplineTolerance = 0
  FixShape = 1
  FullyConstrained = true
  InternalTolerance = 1e-06
  InvalidShape = false
  MakeInternals = false
  MapMode = 5
  Placement = pos=(0,0,0) rot=(1,0,0;1.5708rad)
  Support = -> [XZ_Plane068]
  TreeRank = 0
  ValidateShape = false
  sketch-geometry (1):
    g0: Circle CenterX=0 CenterY=0 CenterZ=0 NormalX=0 NormalY=0 NormalZ=1 AngleXU=0 Radius=3.75
  constraints (2):
    c: Coincident(g0,g-1)
    c: Diameter(g0) = 7.5
FEATURE [PartDesign::Pocket] Pocket051
  AddSubType = 1
  AutoTaperInnerAngle = false
  BaseFeature = -> Pocket050
  CheckUpToFaceLimits = true
  ClaimChildren = false
  Direction = (1,1,1)
  Fit = 0
  FitJoin = 0
  FixShape = 1
  InnerFit = 0
  InnerFitJoin = 0
  InvalidShape = false
  Length = 4
  Length2 = 100
  Linearize = true
  NewSolid = false
  Placement = pos=(0,0,0) rot=(1,0,0;1.5708rad)
  Profile = -> Sketch127
  Refine = true
  Suppress = false
  TaperInnerAngle = 0
  TaperInnerAngleRev = 0
  TreeRank = 0
  Type = 0
  ValidateShape = false
  _ProfileBasedVersion = 1
  _Version = 1
FEATURE [PartDesign::Chamfer] Chamfer040
  AddSubType = 0
  Angle = 45
  Base = -> Pocket051 [Edge24,Edge14]
  BaseFeature = -> Pocket051
  ChamferType = 0
  FixShape = 1
  FlipDirection = false
  InvalidShape = false
  NewSolid = false
  Placement = pos=(0,0,0) rot=(1,0,0;1.5708rad)
  Refine = true
  Size = 0.2
  Size2 = 1
  SupportTransform = false
  Suppress = false
  TreeRank = 0
  UseAllEdges = false
  ValidateShape = false
FEATURE [PartDesign::Chamfer] Chamfer041
  AddSubType = 0
  Angle = 45
  Base = -> Chamfer040 [Edge25]
  BaseFeature = -> Chamfer040
  ChamferType = 0
  FixShape = 1
  FlipDirection = false
  InvalidShape = false
  NewSolid = false
  Placement = pos=(0,0,0) rot=(1,0,0;1.5708rad)
  Refine = true
  Size = 0.2
  Size2 = 1
  SupportTransform = false
  Suppress = false
  TreeRank = 0
  UseAllEdges = false
  ValidateShape = false
FEATURE [PartDesign::Body] Body057  label="PalonnierElastique"
  AutoGroupSolids = false
  ClaimAllChildren = false
  ExportMode = 0
  FixShape = 1
  Group = -> [Sketch123,Pad066,Sketch124,Pad067,Sketch125,Pocket049,Sketch126,Pocket050,Sketch127,Pocket051,Chamfer040,Chamfer041]
  InvalidShape = false
  Origin = -> Origin085
  Placement = pos=(-1.09497e-05,-4.80001,-1.51983e-05) rot=(0,1,0;1.5708rad)
  SingleSolid = true
  Tip = -> Chamfer041
  TreeRank = 0
  ValidateShape = false
  _ExportChildren = -> [Pad066,Pad067,Pocket049,Pocket050,Pocket051,Chamfer040,Chamfer041]
  _GroupVersion = 1
COMPONENT P7 — recipe-attached ("Ventouse20mm", modeled in this document).
Construction recipe (the document's own serialized feature program — sketch geometry with constraints, then the solid features built on it; lengths are millimeters unless a unit is written):

FEATURE [Sketcher::SketchObject] Sketch136
  ArcFitTolerance = 0
  AttachmentSupport = -> [XZ_Plane076]
  ExternalBSplineMaxDegree = 0
  ExternalBSplineTolerance = 0
  FixShape = 1
  FullyConstrained = true
  InternalTolerance = 1e-06
  InvalidShape = false
  MakeInternals = false
  MapMode = 5
  Placement = pos=(0,0,0) rot=(1,0,0;1.5708rad)
  Support = -> [XZ_Plane076]
  TreeRank = 0
  ValidateShape = false
  sketch-geometry (15):
    g0: LineSegment [constr] StartX=0 StartY=0 StartZ=0 EndX=0 EndY=8 EndZ=0
    g1: LineSegment StartX=0 StartY=8 StartZ=0 EndX=-7 EndY=8 EndZ=0
    g2: LineSegment StartX=-7 StartY=8 StartZ=0 EndX=-8.57143 EndY=6 EndZ=0
    g3: LineSegment StartX=-8.57143 StartY=6 StartZ=0 EndX=-11.7143 EndY=10 EndZ=0
    g4: LineSegment StartX=-11.7143 StartY=10 StartZ=0 EndX=-14.8571 EndY=6 EndZ=0
    g5: LineSegment StartX=-14.8571 StartY=6 StartZ=0 EndX=-18 EndY=10 EndZ=0
    g6: LineSegment [constr] StartX=-18 StartY=10 StartZ=0 EndX=-18 EndY=0 EndZ=0
    g7: LineSegment [constr] StartX=-18 StartY=0 StartZ=0 EndX=0 EndY=0 EndZ=0
    g8: LineSegment [constr] StartX=-8.57143 StartY=6 StartZ=0 EndX=-5.42857 EndY=10 EndZ=0
    g9: LineSegment StartX=-15 StartY=4.5 StartZ=0 EndX=-6 EndY=4.5 EndZ=0
    g10: LineSegment StartX=-6 StartY=4.5 StartZ=0 EndX=-6 EndY=2.5 EndZ=0
    g11: LineSegment StartX=-6 StartY=2.5 StartZ=0 EndX=0 EndY=2.5 EndZ=0
    g12: LineSegment StartX=0 StartY=2.5 StartZ=0 EndX=0 EndY=8 EndZ=0
    g13: LineSegment StartX=-18 StartY=10 StartZ=0 EndX=-18 EndY=9.6 EndZ=0
    g14: LineSegment StartX=-15 StartY=4.5 StartZ=0 EndX=-18 EndY=9.6 EndZ=0
  constraints (43):
    c: Coincident(g-1,g0)
    c: PointOnObject(g0,g-2)
    c: Coincident(g0,g1)
    c: Horizontal(g1)
    c: Coincident(g1,g2)
    c: Coincident(g2,g3)
    c: Coincident(g3,g4)
    c: Coincident(g4,g5)
    c: Coincident(g5,g6)
    c: Vertical(g6)
    c: Coincident(g6,g7)
    c: Coincident(g7,g0)
    c: Horizontal(g7)
    c: DistanceY(g0) = 8
    c: DistanceY(g5) = 10
    c: DistanceY(g3) = 10
    c: DistanceX(g5) = -18
    c: Equal(g3,g4)
    c: DistanceY(g2) = 6
    c: Horizontal(g4,g2)
    c: Equal(g4,g5)
    c: DistanceX(g1,g1) = 7
    c: Coincident(g8,g2)
    c: PointOnObject(g1,g8)
    c: Equal(g8,g3)
    c: Horizontal(g8,g3)
    c: Horizontal(g9)
    c: Coincident(g9,g10)
    c: Vertical(g10)
    c: Coincident(g10,g11)
    c: PointOnObject(g11,g0)
    c: Horizontal(g11)
    c: Coincident(g12,g11)
    c: Coincident(g12,g1)
    c: DistanceY(g11) = 2.5
    c: DistanceX(g11,g11) = 6
    c: DistanceY(g9) = 4.5
    c: Coincident(g13,g5)
    c: PointOnObject(g13,g6)
    c: Coincident(g14,g9)
    c: Coincident(g14,g13)
    c: DistanceY(g13,g5) = 0.4
    c: DistanceX(g9,g9) = 9
FEATURE [PartDesign::Revolution] Revolution009
  AddSubType = 0
  Angle = 360
  Axis = (1,0,0)
  Base = (0,0,0)
  ClaimChildren = false
  Fit = 0
  FitJoin = 0
  FixShape = 1
  InnerFit = 0
  InnerFitJoin = 0
  InvalidShape = false
  NewSolid = false
  Placement = pos=(0,0,0) rot=(1,0,0;1.5708rad)
  Profile = -> Sketch136
  ReferenceAxis = -> Sketch136 [H_Axis]
  Refine = true
  Suppress = false
  TreeRank = 0
  ValidateShape = false
  _ProfileBasedVersion = 1
FEATURE [PartDesign::Fillet] Fillet040
  AddSubType = 0
  Base = -> Revolution009 [Edge7,Edge8]
  BaseFeature = -> Revolution009
  FixShape = 1
  InvalidShape = false
  NewSolid = false
  Placement = pos=(0,0,0) rot=(1,0,0;1.5708rad)
  Radius = 0.4
  Refine = true
  SupportTransform = false
  Suppress = false
  TreeRank = 0
  UseAllEdges = false
  ValidateShape = false
FEATURE [PartDesign::Body] Body063  label="Ventouse20mm"
  AutoGroupSolids = false
  ClaimAllChildren = false
  ExportMode = 0
  FixShape = 1
  Group = -> [Sketch136,Revolution009,Fillet040]
  InvalidShape = false
  Origin = -> Origin098
  SingleSolid = true
  Tip = -> Fillet040
  TreeRank = 160
  ValidateShape = false
  _ExportChildren = -> [Revolution009,Fillet040]
  _GroupVersion = 1
COMPONENT P8 — recipe-attached ("MB_150", modeled in this document).
Construction recipe (the document's own serialized feature program — sketch geometry with constraints, then the solid features built on it; lengths are millimeters unless a unit is written):

FEATURE [Sketcher::SketchObject] Sketch200
  ArcFitTolerance = 0
  AttachmentSupport = -> [XZ_Plane115]
  ExternalBSplineMaxDegree = 0
  ExternalBSplineTolerance = 0
  FixShape = 1
  FullyConstrained = true
  InternalTolerance = 1e-06
  InvalidShape = false
  MakeInternals = false
  MapMode = 5
  Placement = pos=(0,0,0) rot=(1,0,0;1.5708rad)
  Support = -> [XZ_Plane115]
  TreeRank = 0
  ValidateShape = false
  sketch-geometry (14):
    g0: ArcOfCircle CenterX=0 CenterY=0 CenterZ=0 NormalX=0 NormalY=0 NormalZ=1 AngleXU=0 Radius=1.25 StartAngle=0 EndAngle=1.5708
    g1: LineSegment StartX=1e-16 StartY=1.25 StartZ=0 EndX=0 EndY=2 EndZ=0
    g2: LineSegment StartX=0 StartY=2 StartZ=0 EndX=1 EndY=2 EndZ=0
    g3: LineSegment [constr] StartX=0 StartY=0 StartZ=0 EndX=5 EndY=5 EndZ=0
    g4: LineSegment StartX=1 StartY=2 StartZ=0 EndX=3.3 EndY=4 EndZ=0
    g5: LineSegment StartX=3.3 StartY=4 StartZ=0 EndX=1.5 EndY=4 EndZ=0
    g6: LineSegment StartX=1.5 StartY=4 StartZ=0 EndX=1.5 EndY=5 EndZ=0
    g7: LineSegment StartX=1.5 StartY=5 StartZ=0 EndX=5 EndY=5 EndZ=0
    g8: LineSegment StartX=5 StartY=5 StartZ=0 EndX=5 EndY=1.5 EndZ=0
    g9: LineSegment StartX=5 StartY=1.5 StartZ=0 EndX=4 EndY=1.5 EndZ=0
    g10: LineSegment StartX=4 StartY=1.5 StartZ=0 EndX=4 EndY=3.3 EndZ=0
    g11: LineSegment StartX=4 StartY=3.3 StartZ=0 EndX=2 EndY=1 EndZ=0
    g12: LineSegment StartX=2 StartY=1 StartZ=0 EndX=2 EndY=0 EndZ=0
    g13: LineSegment StartX=2 StartY=0 StartZ=0 EndX=1.25 EndY=0 EndZ=0
  constraints (41):
    c: Coincident(g0,g-1)
    c: PointOnObject(g0,g-1)
    c: PointOnObject(g0,g-2)
    c: Coincident(g1,g0)
    c: PointOnObject(g1,g-2)
    c: Coincident(g2,g1)
    c: Horizontal(g2)
    c: Coincident(g3,g0)
    c: Angle(g-1,g3) = 0.785398
    c: DistanceX(g3) = 5
    c: Diameter(g0) = 2.5
    c: DistanceX(g2) = 1
    c: Coincident(g4,g2)
    c: Coincident(g5,g4)
    c: Horizontal(g5)
    c: Coincident(g6,g5)
    c: Vertical(g6)
    c: Coincident(g7,g6)
    c: Coincident(g7,g3)
    c: Coincident(g8,g7)
    c: Vertical(g8)
    c: Coincident(g9,g8)
    c: Coincident(g10,g9)
    c: Vertical(g10)
    c: Coincident(g11,g10)
    c: Coincident(g12,g11)
    c: PointOnObject(g12,g-1)
    c: Vertical(g12)
    c: Coincident(g13,g12)
    c: Coincident(g13,g0)
    c: Equal(g12,g2)
    c: Equal(g13,g1)
    c: Horizontal(g7)
    c: Horizontal(g9)
    c: Equal(g6,g9)
    c: Equal(g11,g4)
    c: Equal(g5,g10)
    c: DistanceY(g2,g6) = 3
    c: DistanceX(g6) = 1.5
    c: DistanceY(g6,g6) = 1
    c: DistanceX(g5,g5) = 1.8
FEATURE [PartDesign::Pad] Pad081
  AddSubType = 0
  AlongSketchNormal = false
  AutoTaperInnerAngle = false
  CheckUpToFaceLimits = true
  ClaimChildren = false
  Direction = (0,-1,-2e-16)
  Fit = 0
  FitJoin = 0
  FixShape = 1
  InnerFit = 0
  InnerFitJoin = 0
  InvalidShape = false
  Length = 150
  Length2 = 100
  NewSolid = false
  Profile = -> Sketch200
  Refine = true
  Reversed = true
  Suppress = false
  TaperInnerAngle = 0
  TaperInnerAngleRev = 0
  TreeRank = 0
  Type = 0
  ValidateShape = false
  _ProfileBasedVersion = 0
FEATURE [PartDesign::PolarPattern] PolarPattern013
  AddSubType = 0
  Angle = 360
  Axis = -> Y_Axis115
  BaseFeature = -> Pad081
  CopyShape = false
  FixShape = 1
  InvalidShape = false
  NewSolid = false
  Occurrences = 4
  OriginalSubs = -> [Pad081]
  Originals = -> [Pad081]
  ParallelTransform = true
  Refine = true
  SubTransform = true
  Suppress = false
  TreeRank = 0
  ValidateShape = false
  _Version = 0
FEATURE [PartDesign::CoordinateSystem] Local_CS003
  AttacherType = Attacher::AttachEngine3D
  AttachmentSupport = -> [PolarPattern013]
  FixShape = 1
  InvalidShape = false
  MapMode = 11
  Placement = pos=(3.33e-14,150,-6.66e-14) rot=(0.57735,0.57735,-0.57735;2.0944rad)
  Support = -> [PolarPattern013]
  TreeRank = 0
  ValidateShape = false
FEATURE [PartDesign::Body] Body095  label="MB_150"
  AutoGroupSolids = false
  ClaimAllChildren = false
  ExportMode = 0
  FixShape = 1
  Group = -> [Sketch200,Pad081,PolarPattern013,Local_CS003]
  InvalidShape = false
  Origin = -> Origin185
  SingleSolid = true
  Tip = -> PolarPattern013
  TreeRank = 315
  ValidateShape = false
  _ExportChildren = -> [Pad081,PolarPattern013,Local_CS003]
  _GroupVersion = 1
COMPONENT P9 — recipe-attached ("MB_200", modeled in this document).
Construction recipe (the document's own serialized feature program — sketch geometry with constraints, then the solid features built on it; lengths are millimeters unless a unit is written):

FEATURE [Sketcher::SketchObject] Sketch201
  ArcFitTolerance = 0
  AttachmentSupport = -> [XZ_Plane116]
  ExternalBSplineMaxDegree = 0
  ExternalBSplineTolerance = 0
  FixShape = 1
  FullyConstrained = true
  InternalTolerance = 1e-06
  InvalidShape = false
  MakeInternals = false
  MapMode = 5
  Placement = pos=(0,0,0) rot=(1,0,0;1.5708rad)
  Support = -> [XZ_Plane116]
  TreeRank = 0
  ValidateShape = false
  sketch-geometry (14):
    g0: ArcOfCircle CenterX=0 CenterY=0 CenterZ=0 NormalX=0 NormalY=0 NormalZ=1 AngleXU=0 Radius=1.25 StartAngle=0 EndAngle=1.5708
    g1: LineSegment StartX=1e-16 StartY=1.25 StartZ=0 EndX=0 EndY=2 EndZ=0
    g2: LineSegment StartX=0 StartY=2 StartZ=0 EndX=1 EndY=2 EndZ=0
    g3: LineSegment [constr] StartX=0 StartY=0 StartZ=0 EndX=5 EndY=5 EndZ=0
    g4: LineSegment StartX=1 StartY=2 StartZ=0 EndX=3.3 EndY=4 EndZ=0
    g5: LineSegment StartX=3.3 StartY=4 StartZ=0 EndX=1.5 EndY=4 EndZ=0
    g6: LineSegment StartX=1.5 StartY=4 StartZ=0 EndX=1.5 EndY=5 EndZ=0
    g7: LineSegment StartX=1.5 StartY=5 StartZ=0 EndX=5 EndY=5 EndZ=0
    g8: LineSegment StartX=5 StartY=5 StartZ=0 EndX=5 EndY=1.5 EndZ=0
    g9: LineSegment StartX=5 StartY=1.5 StartZ=0 EndX=4 EndY=1.5 EndZ=0
    g10: LineSegment StartX=4 StartY=1.5 StartZ=0 EndX=4 EndY=3.3 EndZ=0
    g11: LineSegment StartX=4 StartY=3.3 StartZ=0 EndX=2 EndY=1 EndZ=0
    g12: LineSegment StartX=2 StartY=1 StartZ=0 EndX=2 EndY=0 EndZ=0
    g13: LineSegment StartX=2 StartY=0 StartZ=0 EndX=1.25 EndY=0 EndZ=0
  constraints (41):
    c: Coincident(g0,g-1)
    c: PointOnObject(g0,g-1)
    c: PointOnObject(g0,g-2)
    c: Coincident(g1,g0)
    c: PointOnObject(g1,g-2)
    c: Coincident(g2,g1)
    c: Horizontal(g2)
    c: Coincident(g3,g0)
    c: Angle(g-1,g3) = 0.785398
    c: DistanceX(g3) = 5
    c: Diameter(g0) = 2.5
    c: DistanceX(g2) = 1
    c: Coincident(g4,g2)
    c: Coincident(g5,g4)
    c: Horizontal(g5)
    c: Coincident(g6,g5)
    c: Vertical(g6)
    c: Coincident(g7,g6)
    c: Coincident(g7,g3)
    c: Coincident(g8,g7)
    c: Vertical(g8)
    c: Coincident(g9,g8)
    c: Coincident(g10,g9)
    c: Vertical(g10)
    c: Coincident(g11,g10)
    c: Coincident(g12,g11)
    c: PointOnObject(g12,g-1)
    c: Vertical(g12)
    c: Coincident(g13,g12)
    c: Coincident(g13,g0)
    c: Equal(g12,g2)
    c: Equal(g13,g1)
    c: Horizontal(g7)
    c: Horizontal(g9)
    c: Equal(g6,g9)
    c: Equal(g11,g4)
    c: Equal(g5,g10)
    c: DistanceY(g2,g6) = 3
    c: DistanceX(g6) = 1.5
    c: DistanceY(g6,g6) = 1
    c: DistanceX(g5,g5) = 1.8
FEATURE [PartDesign::Pad] Pad082
  AddSubType = 0
  AlongSketchNormal = false
  AutoTaperInnerAngle = false
  CheckUpToFaceLimits = true
  ClaimChildren = false
  Direction = (0,-1,-2e-16)
  Fit = 0
  FitJoin = 0
  FixShape = 1
  InnerFit = 0
  InnerFitJoin = 0
  InvalidShape = false
  Length = 200
  Length2 = 100
  NewSolid = false
  Profile = -> Sketch201
  Refine = true
  Reversed = true
  Suppress = false
  TaperInnerAngle = 0
  TaperInnerAngleRev = 0
  TreeRank = 0
  Type = 0
  ValidateShape = false
  _ProfileBasedVersion = 0
FEATURE [PartDesign::PolarPattern] PolarPattern014
  AddSubType = 0
  Angle = 360
  Axis = -> Y_Axis116
  BaseFeature = -> Pad082
  CopyShape = false
  FixShape = 1
  InvalidShape = false
  NewSolid = false
  Occurrences = 4
  OriginalSubs = -> [Pad082]
  Originals = -> [Pad082]
  ParallelTransform = true
  Refine = true
  SubTransform = true
  Suppress = false
  TreeRank = 0
  ValidateShape = false
  _Version = 0
FEATURE [PartDesign::CoordinateSystem] Local_CS004
  AttacherType = Attacher::AttachEngine3D
  AttachmentSupport = -> [PolarPattern014]
  FixShape = 1
  InvalidShape = false
  MapMode = 11
  Placement = pos=(4.44e-14,200,-8.88e-14) rot=(0.57735,0.57735,-0.57735;2.0944rad)
  Support = -> [PolarPattern014]
  TreeRank = 0
  ValidateShape = false
FEATURE [PartDesign::Body] Body096  label="MB_200"
  AutoGroupSolids = false
  ClaimAllChildren = false
  ExportMode = 0
  FixShape = 1
  Group = -> [Sketch201,Pad082,PolarPattern014,Local_CS004]
  InvalidShape = false
  Origin = -> Origin186
  SingleSolid = true
  Tip = -> PolarPattern014
  TreeRank = 316
  ValidateShape = false
  _ExportChildren = -> [Pad082,PolarPattern014,Local_CS004]
  _GroupVersion = 1
COMPONENT P10 — geometry summary ("MB1r2t"; no construction recipe available for this part):
  bounding box: 98.6 x 87.0 x 64.0 mm
  tessellated surface: 127,664 triangles
  volume: 120319 mm^3 (22% of its bounding box)
COMPONENT P11 — recipe-attached ("Link(ServoMG996R001)", modeled in this document).
Construction recipe (the document's own serialized feature program — sketch geometry with constraints, then the solid features built on it; lengths are millimeters unless a unit is written):

FEATURE [Sketcher::SketchObject] Sketch086
  ArcFitTolerance = 0
  AttachmentSupport = -> [XZ_Plane049]
  ExternalBSplineMaxDegree = 0
  ExternalBSplineTolerance = 0
  FixShape = 1
  FullyConstrained = true
  InternalTolerance = 1e-06
  InvalidShape = false
  MakeInternals = false
  MapMode = 5
  Placement = pos=(0,0,0) rot=(1,0,0;1.5708rad)
  Support = -> [XZ_Plane049]
  TreeRank = 0
  ValidateShape = false
  sketch-geometry (12):
    g0: LineSegment StartX=-37 StartY=-18.5 StartZ=0 EndX=-37 EndY=-16 EndZ=0
    g1: LineSegment StartX=-37 StartY=-16 StartZ=0 EndX=-30 EndY=-16 EndZ=0
    g2: LineSegment StartX=-30 StartY=-16 StartZ=0 EndX=-30 EndY=-8 EndZ=0
    g3: LineSegment StartX=-30 StartY=-8 StartZ=0 EndX=10 EndY=-8 EndZ=0
    g4: LineSegment StartX=10 StartY=-8 StartZ=0 EndX=10 EndY=-16 EndZ=0
    g5: LineSegment StartX=10 StartY=-16 StartZ=0 EndX=17 EndY=-16 EndZ=0
    g6: LineSegment StartX=17 StartY=-16 StartZ=0 EndX=17 EndY=-18.5 EndZ=0
    g7: LineSegment StartX=17 StartY=-18.5 StartZ=0 EndX=10 EndY=-18.5 EndZ=0
    g8: LineSegment StartX=10 StartY=-18.5 StartZ=0 EndX=10 EndY=-47 EndZ=0
    g9: LineSegment StartX=10 StartY=-47 StartZ=0 EndX=-30 EndY=-47 EndZ=0
    g10: LineSegment StartX=-30 StartY=-47 StartZ=0 EndX=-30 EndY=-18.5 EndZ=0
    g11: LineSegment StartX=-30 StartY=-18.5 StartZ=0 EndX=-37 EndY=-18.5 EndZ=0
  constraints (33):
    c: Vertical(g0)
    c: Coincident(g0,g1)
    c: Horizontal(g1)
    c: Coincident(g1,g2)
    c: Vertical(g2)
    c: Coincident(g2,g3)
    c: Horizontal(g3)
    c: Coincident(g3,g4)
    c: Coincident(g4,g5)
    c: Coincident(g5,g6)
    c: Vertical(g6)
    c: Coincident(g6,g7)
    c: Horizontal(g7)
    c: Coincident(g7,g8)
    c: Vertical(g8)
    c: Coincident(g8,g9)
    c: Horizontal(g9)
    c: Coincident(g9,g10)
    c: Coincident(g10,g11)
    c: Coincident(g11,g0)
    c: Horizontal(g11)
    c: Tangent(g4,g8) = -1.5708
    c: Tangent(g10,g2)
    c: Equal(g1,g5)
    c: Tangent(g1,g5)
    c: Equal(g6,g0)
    c: DistanceX(g-1,g3) = 10
    c: DistanceX(g0,g5) = 54
    c: DistanceX(g10,g7) = 40
    c: DistanceY(g9,g-1) = 47
    c: DistanceY(g3,g-1) = 8
    c: DistanceY(g6,g6) = 2.5
    c: DistanceY(g0,g-1) = 18.5
FEATURE [PartDesign::Pad] Pad050
  AddSubType = 0
  AutoTaperInnerAngle = false
  CheckUpToFaceLimits = true
  ClaimChildren = false
  Direction = (1,1,1)
  Fit = 0
  FitJoin = 0
  FixShape = 1
  InnerFit = 0
  InnerFitJoin = 0
  InvalidShape = false
  Length = 20
  Length2 = 100
  Linearize = true
  Midplane = true
  NewSolid = false
  Placement = pos=(0,0,0) rot=(1,0,0;1.5708rad)
  Profile = -> Sketch086
  Refine = true
  Suppress = false
  TaperInnerAngle = 0
  TaperInnerAngleRev = 0
  TreeRank = 0
  Type = 0
  ValidateShape = false
  _ProfileBasedVersion = 1
FEATURE [Sketcher::SketchObject] Sketch087
  ArcFitTolerance = 0
  AttachmentSupport = -> [XY_Plane049]
  ExternalBSplineMaxDegree = 0
  ExternalBSplineTolerance = 0
  FixShape = 1
  FullyConstrained = true
  InternalTolerance = 1e-06
  InvalidShape = false
  MakeInternals = false
  MapMode = 5
  Support = -> [XY_Plane049]
  TreeRank = 0
  ValidateShape = false
  sketch-geometry (4):
    g0: Circle CenterX=14.5 CenterY=5 CenterZ=0 NormalX=0 NormalY=0 NormalZ=1 AngleXU=0 Radius=2
    g1: Circle CenterX=14.5 CenterY=-5 CenterZ=0 NormalX=0 NormalY=0 NormalZ=1 AngleXU=0 Radius=2
    g2: Circle CenterX=-34.5 CenterY=5 CenterZ=0 NormalX=0 NormalY=0 NormalZ=1 AngleXU=0 Radius=2
    g3: Circle CenterX=-34.5 CenterY=-5 CenterZ=0 NormalX=0 NormalY=0 NormalZ=1 AngleXU=0 Radius=2
  constraints (10):
    c: Equal(g2,g3)
    c: Equal(g3,g1)
    c: Equal(g1,g0)
    c: Symmetric(g0,g1,g-1)
    c: Symmetric(g2,g3,g-1)
    c: Horizontal(g2,g0)
    c: Diameter(g0) = 4
    c: DistanceY(g1,g0) = 10
    c: DistanceX(g2,g0) = 49
    c: DistanceX(g-1,g0) = 14.5
FEATURE [PartDesign::Pocket] Pocket033
  AddSubType = 1
  AutoTaperInnerAngle = false
  BaseFeature = -> Pad050
  CheckUpToFaceLimits = true
  ClaimChildren = false
  Direction = (1,1,1)
  Fit = 0
  FitJoin = 0
  FixShape = 1
  InnerFit = 0
  InnerFitJoin = 0
  InvalidShape = false
  Length = 5
  Length2 = 100
  Linearize = true
  NewSolid = false
  Placement = pos=(0,0,0) rot=(1,0,0;1.5708rad)
  Profile = -> Sketch087
  Refine = true
  Suppress = false
  TaperInnerAngle = 0
  TaperInnerAngleRev = 0
  TreeRank = 0
  Type = 1
  ValidateShape = false
  _ProfileBasedVersion = 1
  _Version = 0
FEATURE [PartDesign::Fillet] Fillet024
  AddSubType = 0
  Base = -> Pocket033 [Edge28,Edge19,Edge4,Edge3]
  BaseFeature = -> Pocket033
  FixShape = 1
  InvalidShape = false
  NewSolid = false
  Placement = pos=(0,0,0) rot=(1,0,0;1.5708rad)
  Radius = 1
  Refine = true
  SupportTransform = false
  Suppress = false
  TreeRank = 0
  UseAllEdges = false
  ValidateShape = false
FEATURE [PartDesign::Body] Body041  label="ServoBody001"
  AutoGroupSolids = false
  ClaimAllChildren = false
  ExportMode = 0
  FixShape = 1
  Group = -> [Sketch086,Pad050,Sketch087,Pocket033,Fillet024]
  InvalidShape = false
  Origin = -> Origin062
  SingleSolid = true
  Tip = -> Fillet024
  TreeRank = 0
  ValidateShape = false
  _ExportChildren = -> [Pad050,Pocket033,Fillet024]
  _GroupVersion = 1
FEATURE [Sketcher::SketchObject] Sketch090
  ArcFitTolerance = 0
  AttachmentOffset = pos=(0,0,-2) rot=(0,0,1;0rad)
  AttachmentSupport = -> [XY_Plane051]
  ExternalBSplineMaxDegree = 0
  ExternalBSplineTolerance = 0
  FixShape = 1
  FullyConstrained = true
  InternalTolerance = 1e-06
  InvalidShape = false
  MakeInternals = false
  MapMode = 5
  Placement = pos=(0,0,-2) rot=(0,0,1;0rad)
  Support = -> [XY_Plane051]
  TreeRank = 0
  ValidateShape = false
  sketch-geometry (1):
    g0: Circle CenterX=0 CenterY=0 CenterZ=0 NormalX=0 NormalY=0 NormalZ=1 AngleXU=0 Radius=3
  constraints (2):
    c: Coincident(g0,g-1)
    c: Diameter(g0) = 6
FEATURE [PartDesign::Pad] Pad053
  AddSubType = 0
  AutoTaperInnerAngle = false
  CheckUpToFaceLimits = true
  ClaimChildren = false
  Direction = (1,1,1)
  Fit = 0
  FitJoin = 0
  FixShape = 1
  InnerFit = 0
  InnerFitJoin = 0
  InvalidShape = false
  Length = 10
  Length2 = 100
  Linearize = true
  NewSolid = false
  Profile = -> Sketch090
  Refine = true
  Reversed = true
  Suppress = false
  TaperInnerAngle = 0
  TaperInnerAngleRev = 0
  TreeRank = 0
  Type = 0
  ValidateShape = false
  _ProfileBasedVersion = 1
FEATURE [PartDesign::Chamfer] Chamfer029
  AddSubType = 0
  Angle = 45
  Base = -> Pad053 [Edge2]
  BaseFeature = -> Pad053
  ChamferType = 0
  FixShape = 1
  FlipDirection = false
  InvalidShape = false
  NewSolid = false
  Refine = true
  Size = 0.5
  Size2 = 1
  SupportTransform = false
  Suppress = false
  TreeRank = 0
  UseAllEdges = false
  ValidateShape = false
FEATURE [PartDesign::Body] Body043  label="ServoAxis001"
  AutoGroupSolids = false
  ClaimAllChildren = false
  ExportMode = 0
  FixShape = 1
  Group = -> [Sketch090,Pad053,Chamfer029]
  InvalidShape = false
  Origin = -> Origin064
  SingleSolid = true
  Tip = -> Chamfer029
  TreeRank = 0
  ValidateShape = false
  _ExportChildren = -> [Pad053,Chamfer029]
  _GroupVersion = 1
COMPONENT P12 — recipe-attached ("ServoMG-SG90", modeled in this document).
Construction recipe (the document's own serialized feature program — sketch geometry with constraints, then the solid features built on it; lengths are millimeters unless a unit is written):

FEATURE [Sketcher::SketchObject] Sketch162
  ArcFitTolerance = 0
  AttachmentSupport = -> [XY_Plane096]
  ExternalBSplineMaxDegree = 0
  ExternalBSplineTolerance = 0
  FixShape = 1
  FullyConstrained = true
  InternalTolerance = 1e-06
  InvalidShape = false
  MakeInternals = false
  MapMode = 5
  Support = -> [XY_Plane096]
  TreeRank = 36
  ValidateShape = false
  sketch-geometry (12):
    g0: LineSegment StartX=-17 StartY=2.106e-12 StartZ=0 EndX=-21.7 EndY=5.127e-13 EndZ=0
    g1: LineSegment StartX=-21.7 StartY=5.127e-13 StartZ=0 EndX=-21.7 EndY=-2.4 EndZ=0
    g2: LineSegment StartX=-21.7 StartY=-2.4 StartZ=0 EndX=-17 EndY=-2.4 EndZ=0
    g3: LineSegment StartX=-17 StartY=-2.4 StartZ=0 EndX=-17 EndY=-6.8 EndZ=0
    g4: LineSegment StartX=-17 StartY=-6.8 StartZ=0 EndX=6 EndY=-6.8 EndZ=0
    g5: LineSegment StartX=6 StartY=-6.8 StartZ=0 EndX=6 EndY=-2.4 EndZ=0
    g6: LineSegment StartX=6 StartY=-2.4 StartZ=0 EndX=10.7 EndY=-2.4 EndZ=0
    g7: LineSegment StartX=10.7 StartY=-2.4 StartZ=0 EndX=10.7 EndY=1.124e-12 EndZ=0
    g8: LineSegment StartX=10.7 StartY=1.1239e-12 StartZ=0 EndX=6 EndY=-1.9734e-12 EndZ=0
    g9: LineSegment StartX=6 StartY=-1.9734e-12 StartZ=0 EndX=6 EndY=15.8 EndZ=0
    g10: LineSegment StartX=6 StartY=15.8 StartZ=0 EndX=-17 EndY=15.8 EndZ=0
    g11: LineSegment StartX=-17 StartY=15.8 StartZ=0 EndX=-17 EndY=2.1068e-12 EndZ=0
  constraints (36):
    c: PointOnObject(g0,g-1)
    c: PointOnObject(g0,g-1)
    c: Coincident(g0,g1)
    c: Vertical(g1)
    c: Coincident(g1,g2)
    c: Horizontal(g2)
    c: Coincident(g2,g3)
    c: Vertical(g3)
    c: Coincident(g3,g4)
    c: Horizontal(g4)
    c: Coincident(g4,g5)
    c: Vertical(g5)
    c: Coincident(g5,g6)
    c: Horizontal(g6)
    c: Coincident(g6,g7)
    c: PointOnObject(g7,g-1)
    c: Vertical(g7)
    c: Coincident(g7,g8)
    c: PointOnObject(g8,g-1)
    c: Coincident(g8,g9)
    c: Vertical(g9)
    c: Coincident(g9,g10)
    c: Horizontal(g10)
    c: Coincident(g10,g11)
    c: Coincident(g11,g0)
    c: Vertical(g11)
    c: Equal(g0,g2)
    c: Equal(g2,g6)
    c: Equal(g6,g8)
    c: DistanceX(g4) = 6
    c: DistanceX(g4,g4) = 23
    c: DistanceX(g1,g6) = 32.4
    c: DistanceY(g3,g3) = 4.4
    c: DistanceY(g1,g1) = 2.4
    c: Equal(g7,g1)
    c: DistanceY(g9,g9) = 15.8
FEATURE [PartDesign::Pad] Pad068
  AddSubType = 0
  AlongSketchNormal = false
  AutoTaperInnerAngle = false
  CheckUpToFaceLimits = true
  ClaimChildren = false
  Direction = (0,0,1)
  Fit = 0
  FitJoin = 0
  FixShape = 1
  InnerFit = 0
  InnerFitJoin = 0
  InvalidShape = false
  Length = 12
  Length2 = 100
  Linearize = true
  Midplane = true
  NewSolid = false
  Profile = -> Sketch162
  Refine = true
  Suppress = false
  TaperInnerAngle = 0
  TaperInnerAngleRev = 0
  TreeRank = 37
  Type = 0
  ValidateShape = false
  _ProfileBasedVersion = 1
FEATURE [Sketcher::SketchObject] Sketch163
  ArcFitTolerance = 0
  AttachmentSupport = -> [Pad068]
  ExternalBSplineMaxDegree = 0
  ExternalBSplineTolerance = 0
  FixShape = 1
  FullyConstrained = true
  InternalTolerance = 1e-06
  InvalidShape = false
  MakeInternals = false
  MapMode = 5
  Placement = pos=(0,-6.8,0) rot=(1,0,0;1.5708rad)
  Support = -> [Pad068]
  TreeRank = 38
  ValidateShape = false
  sketch-geometry (4):
    g0: ArcOfCircle CenterX=-5.554e-13 CenterY=-7.838e-13 CenterZ=0 NormalX=0 NormalY=0 NormalZ=1 AngleXU=0 Radius=6 StartAngle=3.57137 EndAngle=8.995
    g1: ArcOfCircle CenterX=-6 CenterY=4.736e-13 CenterZ=0 NormalX=0 NormalY=0 NormalZ=1 AngleXU=0 Radius=2.5 StartAngle=1.5708 EndAngle=4.71239
    g2: LineSegment StartX=-6 StartY=2.5 StartZ=0 EndX=-5.45436 EndY=2.5 EndZ=0
    g3: LineSegment StartX=-6 StartY=-2.5 StartZ=0 EndX=-5.45436 EndY=-2.5 EndZ=0
  constraints (11):
    c: Coincident(g0,g-1)
    c: PointOnObject(g1,g-1)
    c: Coincident(g2,g0)
    c: Coincident(g3,g0)
    c: Horizontal(g3)
    c: Horizontal(g2)
    c: Tangent(g2,g1) = 1.5708
    c: Tangent(g3,g1) = -1.5708
    c: Radius(g0) = 6
    c: DistanceY(g1,g1) = 5
    c: DistanceX(g1,g0) = 6
FEATURE [PartDesign::Pad] Pad069
  AddSubType = 0
  AlongSketchNormal = false
  AutoTaperInnerAngle = false
  BaseFeature = -> Pad068
  CheckUpToFaceLimits = true
  ClaimChildren = false
  Direction = (0,-1,2e-16)
  Fit = 0
  FitJoin = 0
  FixShape = 1
  InnerFit = 0
  InnerFitJoin = 0
  InvalidShape = false
  Length = 4
  Length2 = 100
  Linearize = true
  NewSolid = false
  Profile = -> Sketch163
  Refine = true
  Suppress = false
  TaperInnerAngle = 0
  TaperInnerAngleRev = 0
  TreeRank = 39
  Type = 0
  ValidateShape = false
  _ProfileBasedVersion = 1
FEATURE [Sketcher::SketchObject] Sketch164
  ArcFitTolerance = 0
  AttachmentSupport = -> [XZ_Plane096]
  ExternalBSplineMaxDegree = 0
  ExternalBSplineTolerance = 0
  ExternalGeometry = -> [Pad069]
  FixShape = 1
  FullyConstrained = true
  InternalTolerance = 1e-06
  InvalidShape = false
  MakeInternals = false
  MapMode = 5
  Placement = pos=(0,0,0) rot=(1,0,0;1.5708rad)
  Support = -> [XZ_Plane096]
  TreeRank = 40
  ValidateShape = false
  sketch-geometry (4):
    g0: Circle CenterX=-19.25 CenterY=-8.88e-14 CenterZ=0 NormalX=0 NormalY=0 NormalZ=1 AngleXU=0 Radius=1
    g1: Circle CenterX=8.25 CenterY=8.765e-12 CenterZ=0 NormalX=0 NormalY=0 NormalZ=1 AngleXU=0 Radius=1
    g2: LineSegment [constr] StartX=-21.7 StartY=-6 StartZ=0 EndX=10.7 EndY=6 EndZ=0
    g3: GeomPoint [constr] X=-5.5 Y=5.2304e-12 Z=0
  constraints (8):
    c: PointOnObject(g0,g-1)
    c: DistanceX(g0,g1) = 27.5
    c: Equal(g0,g1)
    c: Diameter(g0) = 2
    c: Coincident(g2,g-3)
    c: Coincident(g2,g-4)
    c: Symmetric(g-4,g-3,g3)
    c: Symmetric(g0,g1,g3)
FEATURE [PartDesign::Pocket] Pocket052
  AddSubType = 1
  AutoTaperInnerAngle = false
  BaseFeature = -> Pad069
  CheckUpToFaceLimits = true
  ClaimChildren = false
  Direction = (1,1,1)
  Fit = 0
  FitJoin = 0
  FixShape = 1
  InnerFit = 0
  InnerFitJoin = 0
  InvalidShape = false
  Length = 5
  Length2 = 100
  Linearize = true
  NewSolid = false
  Profile = -> Sketch164
  Refine = true
  Reversed = true
  Suppress = false
  TaperInnerAngle = 0
  TaperInnerAngleRev = 0
  TreeRank = 41
  Type = 1
  ValidateShape = false
  _ProfileBasedVersion = 1
  _Version = 1
FEATURE [PartDesign::Body] Body076  label="BodyServo90S"
  AutoGroupSolids = false
  ClaimAllChildren = false
  ExportMode = 0
  FixShape = 1
  Group = -> [Sketch162,Pad068,Sketch163,Pad069,Sketch164,Pocket052]
  InvalidShape = false
  Origin = -> Origin
  SingleSolid = true
  Tip = -> Pocket052
  TreeRank = 35
  ValidateShape = false
  _ExportChildren = -> [Pad068,Pad069,Pocket052]
  _GroupVersion = 1
FEATURE [Part::SubShapeBinder] Import  label="Import(Pocket052)"
  BindCopyOnChange = 0
  BindMode = 0
  ClaimChildren = false
  Context = -> Group007 [Part.Body077.Import.]
  EdgeTolerance = 1e-06
  FillStyle = 0
  FixShape = 1
  Fuse = false
  InvalidShape = false
  MakeFace = false
  MergeEdges = true
  OffsetFill = false
  OffsetIntersection = false
  OffsetJoinType = 0
  OffsetOpenResult = false
  Outline = false
  PartialLoad = false
  Relative = true
  SplitEdges = false
  Support = -> [Body076[Pocket052.]]
  TightBound = false
  TreeRank = 52
  ValidateShape = false
  _Version = 8
FEATURE [Sketcher::SketchObject] Sketch165
  ArcFitTolerance = 0
  AttachmentSupport = -> [Import]
  ExternalBSplineMaxDegree = 0
  ExternalBSplineTolerance = 0
  FixShape = 1
  FullyConstrained = true
  InternalTolerance = 1e-06
  InvalidShape = false
  MakeInternals = false
  MapMode = 5
  Placement = pos=(0,-10.8,2.3e-15) rot=(1,0,0;1.5708rad)
  Support = -> [Import]
  TreeRank = 53
  ValidateShape = false
  sketch-geometry (1):
    g0: Circle CenterX=0 CenterY=0 CenterZ=0 NormalX=0 NormalY=0 NormalZ=1 AngleXU=0 Radius=2.25
  constraints (2):
    c: Coincident(g0,g-1)
    c: Diameter(g0) = 4.5
FEATURE [PartDesign::Pad] Pad070
  AddSubType = 0
  AlongSketchNormal = false
  AutoTaperInnerAngle = false
  CheckUpToFaceLimits = true
  ClaimChildren = false
  Direction = (0,-1,2e-16)
  Fit = 0
  FitJoin = 0
  FixShape = 1
  InnerFit = 0
  InnerFitJoin = 0
  InvalidShape = false
  Length = 2.4
  Length2 = 100
  Linearize = true
  NewSolid = false
  Profile = -> Sketch165
  Refine = true
  Suppress = false
  TaperInnerAngle = 0
  TaperInnerAngleRev = 0
  TreeRank = 54
  Type = 0
  ValidateShape = false
  _ProfileBasedVersion = 1
FEATURE [PartDesign::Body] Body077  label="AxleServo90S"
  AutoGroupSolids = false
  ClaimAllChildren = false
  ExportMode = 0
  FixShape = 1
  Group = -> [Import,Sketch165,Pad070]
  InvalidShape = false
  Origin = -> Origin162
  SingleSolid = true
  Tip = -> Pad070
  TreeRank = 51
  ValidateShape = false
  _ExportChildren = -> [Import,Pad070]
  _GroupVersion = 1
FEATURE [Part::SubShapeBinder] Import001  label="Import001(Pocket052)"
  BindCopyOnChange = 0
  BindMode = 0
  ClaimChildren = false
  Context = -> <external ../table_2022.FCStd>#Link005 [Link008.Part031.Link106.Body078.Import001.]
  EdgeTolerance = 1e-06
  FillStyle = 0
  FixShape = 1
  Fuse = false
  InvalidShape = false
  MakeFace = false
  MergeEdges = true
  OffsetFill = false
  OffsetIntersection = false
  OffsetJoinType = 0
  OffsetOpenResult = false
  Outline = false
  PartialLoad = false
  Relative = true
  SplitEdges = false
  Support = -> [Body076[Pocket052.]]
  TightBound = false
  TreeRank = 65
  ValidateShape = false
  _Version = 8
FEATURE [Sketcher::SketchObject] Sketch166
  ArcFitTolerance = 0
  AttachmentSupport = -> [Import001]
  ExternalBSplineMaxDegree = 0
  ExternalBSplineTolerance = 0
  FixShape = 1
  FullyConstrained = true
  InternalTolerance = 1e-06
  InvalidShape = false
  MakeInternals = false
  MapMode = 5
  Placement = pos=(6,0,0) rot=(0.57735,0.57735,0.57735;2.0944rad)
  Support = -> [Import001]
  TreeRank = 74
  ValidateShape = false
  sketch-geometry (3):
    g0: Circle CenterX=10 CenterY=-9.4173e-12 CenterZ=0 NormalX=0 NormalY=0 NormalZ=1 AngleXU=0 Radius=0.5
    g1: Circle CenterX=10 CenterY=1 CenterZ=0 NormalX=0 NormalY=0 NormalZ=1 AngleXU=0 Radius=0.5
    g2: Circle CenterX=10 CenterY=-1 CenterZ=0 NormalX=0 NormalY=0 NormalZ=1 AngleXU=0 Radius=0.5
  constraints (9):
    c: PointOnObject(g0,g-1)
    c: Tangent(g1,g0)
    c: Tangent(g2,g0)
    c: Vertical(g2,g0)
    c: Vertical(g0,g1)
    c: Equal(g1,g0)
    c: Equal(g1,g2)
    c: Diameter(g1) = 1
    c: DistanceX(g0) = 10
FEATURE [PartDesign::Pad] Pad071
  AddSubType = 0
  AlongSketchNormal = false
  AutoTaperInnerAngle = false
  CheckUpToFaceLimits = true
  ClaimChildren = false
  Direction = (1,0,0)
  Fit = 0
  FitJoin = 0
  FixShape = 1
  InnerFit = 0
  InnerFitJoin = 0
  InvalidShape = false
  Length = 10
  Length2 = 100
  Linearize = true
  NewSolid = false
  Profile = -> Sketch166
  Refine = true
  Suppress = false
  TaperInnerAngle = 0
  TaperInnerAngleRev = 0
  TreeRank = 75
  Type = 0
  ValidateShape = false
  _ProfileBasedVersion = 1
FEATURE [PartDesign::Body] Body078  label="Cables001"
  AutoGroupSolids = true
  ClaimAllChildren = false
  ExportMode = 0
  FixShape = 1
  Group = -> [Import001,Sketch166,Pad071]
  InvalidShape = false
  Origin = -> Origin163
  Tip = -> Pad071
  TreeRank = 64
  ValidateShape = false
  _ExportChildren = -> [Import001,Pad071]
  _GroupVersion = 1
COMPONENT P13 — recipe-attached ("MR148", modeled in this document).
Construction recipe (the document's own serialized feature program — sketch geometry with constraints, then the solid features built on it; lengths are millimeters unless a unit is written):

FEATURE [Sketcher::SketchObject] Sketch118
  ArcFitTolerance = 0
  AttachmentSupport = -> [XZ_Plane064]
  ExternalBSplineMaxDegree = 0
  ExternalBSplineTolerance = 0
  FixShape = 1
  FullyConstrained = true
  InternalTolerance = 1e-06
  InvalidShape = false
  MakeInternals = false
  MapMode = 5
  Placement = pos=(0,0,0) rot=(1,0,0;1.5708rad)
  Support = -> [XZ_Plane064]
  TreeRank = 0
  ValidateShape = false
  sketch-geometry (12):
    g0: LineSegment StartX=-6 StartY=2.67e-14 StartZ=0 EndX=-7 EndY=-1.177e-13 EndZ=0
    g1: LineSegment StartX=-7 StartY=-1.177e-13 StartZ=0 EndX=-7 EndY=4 EndZ=0
    g2: LineSegment StartX=-7 StartY=4 StartZ=0 EndX=-6 EndY=4 EndZ=0
    g3: LineSegment StartX=-6 StartY=4 StartZ=0 EndX=-6 EndY=3.6 EndZ=0
    g4: LineSegment StartX=-6 StartY=3.6 StartZ=0 EndX=-5 EndY=3.6 EndZ=0
    g5: LineSegment StartX=-5 StartY=3.6 StartZ=0 EndX=-5 EndY=4 EndZ=0
    g6: LineSegment StartX=-5 StartY=4 StartZ=0 EndX=-4 EndY=4 EndZ=0
    g7: LineSegment StartX=-4 StartY=4 StartZ=0 EndX=-4 EndY=0 EndZ=0
    g8: LineSegment StartX=-4 StartY=0 StartZ=0 EndX=-5 EndY=0 EndZ=0
    g9: LineSegment StartX=-5 StartY=0 StartZ=0 EndX=-5 EndY=0.4 EndZ=0
    g10: LineSegment StartX=-5 StartY=0.4 StartZ=0 EndX=-6 EndY=0.4 EndZ=0
    g11: LineSegment StartX=-6 StartY=0.4 StartZ=0 EndX=-6 EndY=2.67e-14 EndZ=0
  constraints (36):
    c: PointOnObject(g0,g-1)
    c: PointOnObject(g0,g-1)
    c: Coincident(g0,g1)
    c: Vertical(g1)
    c: Coincident(g1,g2)
    c: Horizontal(g2)
    c: Coincident(g2,g3)
    c: Vertical(g3)
    c: Coincident(g3,g4)
    c: Horizontal(g4)
    c: Coincident(g4,g5)
    c: Vertical(g5)
    c: Coincident(g5,g6)
    c: Horizontal(g6)
    c: Coincident(g6,g7)
    c: PointOnObject(g7,g-1)
    c: Vertical(g7)
    c: Coincident(g7,g8)
    c: PointOnObject(g8,g-1)
    c: Coincident(g8,g9)
    c: Vertical(g9)
    c: Coincident(g9,g10)
    c: Horizontal(g10)
    c: Coincident(g10,g11)
    c: Coincident(g11,g0)
    c: Vertical(g11)
    c: DistanceX(g7) = -4
    c: DistanceX(g0) = -7
    c: Equal(g8,g0)
    c: Equal(g2,g6)
    c: Equal(g4,g10)
    c: Equal(g3,g11)
    c: DistanceY(g3,g3) = 0.4
    c: DistanceX(g8,g8) = 1
    c: DistanceY(g1,g1) = 4
    c: PointOnObject(g2,g6)
FEATURE [PartDesign::Revolution] Revolution007
  AddSubType = 0
  Angle = 360
  Axis = (0,-2e-16,1)
  Base = (0,0,0)
  ClaimChildren = false
  Fit = 0
  FitJoin = 0
  FixShape = 1
  InnerFit = 0
  InnerFitJoin = 0
  InvalidShape = false
  NewSolid = false
  Placement = pos=(0,0,0) rot=(1,0,0;1.5708rad)
  Profile = -> Sketch118
  ReferenceAxis = -> Sketch118 [V_Axis]
  Refine = true
  Suppress = false
  TreeRank = 0
  ValidateShape = false
  _ProfileBasedVersion = 0
FEATURE [PartDesign::Body] Body054  label="CoreMR148"
  AutoGroupSolids = false
  ClaimAllChildren = false
  ExportMode = 0
  FixShape = 1
  Group = -> [Sketch118,Revolution007]
  InvalidShape = false
  Origin = -> Origin081
  SingleSolid = true
  Tip = -> Revolution007
  TreeRank = 0
  ValidateShape = false
  _ExportChildren = -> [Revolution007]
  _GroupVersion = 1
FEATURE [Sketcher::SketchObject] Sketch119
  ArcFitTolerance = 0
  AttachmentSupport = -> [XZ_Plane065]
  ExternalBSplineMaxDegree = 0
  ExternalBSplineTolerance = 0
  FixShape = 1
  FullyConstrained = true
  InternalTolerance = 1e-06
  InvalidShape = false
  MakeInternals = false
  MapMode = 5
  Placement = pos=(0,0,0) rot=(1,0,0;1.5708rad)
  Support = -> [XZ_Plane065]
  TreeRank = 0
  ValidateShape = false
  sketch-geometry (4):
    g0: LineSegment StartX=-6 StartY=4 StartZ=0 EndX=-5 EndY=4 EndZ=0
    g1: LineSegment StartX=-5 StartY=4 StartZ=0 EndX=-5 EndY=0 EndZ=0
    g2: LineSegment StartX=-5 StartY=0 StartZ=0 EndX=-6 EndY=0 EndZ=0
    g3: LineSegment StartX=-6 StartY=0 StartZ=0 EndX=-6 EndY=4 EndZ=0
  constraints (12):
    c: Coincident(g0,g1)
    c: Coincident(g1,g2)
    c: Coincident(g2,g3)
    c: Coincident(g3,g0)
    c: Horizontal(g0)
    c: Horizontal(g2)
    c: Vertical(g1)
    c: Vertical(g3)
    c: PointOnObject(g1,g-1)
    c: DistanceY(g3,g3) = 4
    c: DistanceX(g1) = -5
    c: DistanceX(g2) = -6
FEATURE [PartDesign::Revolution] Revolution008
  AddSubType = 0
  Angle = 360
  Axis = (0,-2e-16,1)
  Base = (0,0,0)
  ClaimChildren = false
  Fit = 0
  FitJoin = 0
  FixShape = 1
  InnerFit = 0
  InnerFitJoin = 0
  InvalidShape = false
  NewSolid = false
  Placement = pos=(0,0,0) rot=(1,0,0;1.5708rad)
  Profile = -> Sketch119
  ReferenceAxis = -> Sketch119 [V_Axis]
  Refine = true
  Suppress = false
  TreeRank = 0
  ValidateShape = false
  _ProfileBasedVersion = 0
FEATURE [PartDesign::Body] Body055  label="Sleeve"
  AutoGroupSolids = false
  ClaimAllChildren = false
  ExportMode = 0
  FixShape = 1
  Group = -> [Sketch119,Revolution008]
  InvalidShape = false
  Origin = -> Origin082
  SingleSolid = true
  Tip = -> Revolution008
  TreeRank = 0
  ValidateShape = false
  _ExportChildren = -> [Revolution008]
  _GroupVersion = 1
COMPONENT P14 — recipe-attached ("YDLidar G2", modeled in this document).
Construction recipe (the document's own serialized feature program — sketch geometry with constraints, then the solid features built on it; lengths are millimeters unless a unit is written):

FEATURE [Sketcher::SketchObject] Sketch196
  ArcFitTolerance = 0
  AttachmentSupport = -> [XZ_Plane111]
  ExternalBSplineMaxDegree = 0
  ExternalBSplineTolerance = 0
  FixShape = 1
  FullyConstrained = true
  InternalTolerance = 1e-06
  InvalidShape = false
  MakeInternals = false
  MapMode = 5
  Placement = pos=(0,0,0) rot=(1,0,0;1.5708rad)
  Support = -> [XZ_Plane111]
  TreeRank = 121
  ValidateShape = false
  sketch-geometry (8):
    g0: LineSegment StartX=0 StartY=0 StartZ=0 EndX=36.85 EndY=0 EndZ=0
    g1: LineSegment StartX=36.85 StartY=0 StartZ=0 EndX=36.3694 EndY=21.5 EndZ=0
    g2: LineSegment StartX=36.3694 StartY=21.5 StartZ=0 EndX=34.3694 EndY=21.5 EndZ=0
    g3: LineSegment StartX=34.3694 StartY=21.5 StartZ=0 EndX=34.3694 EndY=22.5 EndZ=0
    g4: LineSegment StartX=34.3694 StartY=22.5 StartZ=0 EndX=0 EndY=22.5 EndZ=0
    g5: LineSegment StartX=0 StartY=22.5 StartZ=0 EndX=0 EndY=0 EndZ=0
    g6: LineSegment [constr] StartX=36.3694 StartY=21.5 StartZ=0 EndX=35.9 EndY=42.5 EndZ=0
    g7: LineSegment [constr] StartX=35.9 StartY=42.5 StartZ=0 EndX=0 EndY=42.5 EndZ=0
  constraints (23):
    c: Coincident(g-1,g0)
    c: PointOnObject(g0,g-1)
    c: Coincident(g0,g1)
    c: Coincident(g1,g2)
    c: Horizontal(g2)
    c: Coincident(g2,g3)
    c: Vertical(g3)
    c: Coincident(g3,g4)
    c: Horizontal(g4)
    c: Coincident(g4,g5)
    c: Coincident(g5,g0)
    c: Vertical(g5)
    c: DistanceX(g0,g0) = 36.85
    c: Coincident(g6,g1)
    c: Coincident(g7,g6)
    c: Horizontal(g7)
    c: DistanceY(g7) = 42.5
    c: Parallel(g6,g1)
    c: DistanceX(g7,g7) = 35.9
    c: DistanceY(g1) = 21.5
    c: DistanceY(g3,g3) = 1
    c: DistanceX(g2,g2) = 2
    c: PointOnObject(g7,g-2)
FEATURE [PartDesign::Revolution] Revolution017
  AddSubType = 0
  Angle = 360
  Axis = (0,-2e-16,1)
  Base = (0,0,0)
  ClaimChildren = false
  Fit = 0
  FitJoin = 0
  FixShape = 1
  InnerFit = 0
  InnerFitJoin = 0
  InvalidShape = false
  NewSolid = false
  Placement = pos=(0,0,0) rot=(1,0,0;1.5708rad)
  Profile = -> Sketch196
  ReferenceAxis = -> Sketch196 [V_Axis]
  Refine = true
  Reversed = true
  Suppress = false
  TreeRank = 0
  ValidateShape = false
  _ProfileBasedVersion = 1
FEATURE [PartDesign::Body] Body092  label="Base G2"
  AutoGroupSolids = false
  ClaimAllChildren = false
  ExportMode = 0
  FixShape = 1
  Group = -> [Sketch196,Revolution017]
  InvalidShape = false
  Origin = -> Origin183
  SingleSolid = true
  Tip = -> Revolution017
  TreeRank = 0
  ValidateShape = false
  _ExportChildren = -> [Revolution017]
  _GroupVersion = 1
FEATURE [PartDesign::SubShapeBinder] Binder  label="Binder(Sketch004)"
  BindCopyOnChange = 0
  BindMode = 0
  ClaimChildren = false
  Context = -> Group011 [Part002.Body093.Binder.]
  EdgeTolerance = 1e-06
  FillStyle = 0
  FixShape = 1
  Fuse = false
  InvalidShape = false
  MakeFace = true
  MergeEdges = true
  OffsetFill = false
  OffsetIntersection = false
  OffsetJoinType = 0
  OffsetOpenResult = false
  Outline = false
  PartialLoad = false
  Refine = true
  Relative = true
  SplitEdges = false
  Support = -> [Body092[Sketch196.]]
  TightBound = false
  TreeRank = 0
  ValidateShape = false
  _Version = 8
FEATURE [Sketcher::SketchObject] Sketch197
  ArcFitTolerance = 0
  AttachmentSupport = -> [XZ_Plane112]
  ExternalBSplineMaxDegree = 0
  ExternalBSplineTolerance = 0
  FixShape = 1
  FullyConstrained = false
  InternalTolerance = 1e-06
  InvalidShape = false
  MakeInternals = false
  MapMode = 5
  Placement = pos=(0,0,0) rot=(1,0,0;1.5708rad)
  Support = -> [XZ_Plane112]
  TreeRank = 128
  ValidateShape = false
  sketch-geometry (4):
    g0: LineSegment StartX=0 StartY=22.5 StartZ=0 EndX=36.3471 EndY=22.5 EndZ=0
    g1: LineSegment StartX=36.3471 StartY=22.5 StartZ=0 EndX=35.9 EndY=42.5 EndZ=0
    g2: LineSegment StartX=35.9 StartY=42.5 StartZ=0 EndX=0 EndY=42.5 EndZ=0
    g3: LineSegment StartX=0 StartY=42.5 StartZ=0 EndX=0 EndY=22.5 EndZ=0
  constraints (8):
    c: Horizontal(g0)
    c: Coincident(g0,g1)
    c: Coincident(g1,g2)
    c: PointOnObject(g2,g-2)
    c: Horizontal(g2)
    c: Coincident(g2,g3)
    c: Coincident(g3,g0)
    c: DistanceY(g2) = 42.5
FEATURE [PartDesign::Revolution] Revolution001
  AddSubType = 0
  Angle = 360
  Axis = (0,-2e-16,1)
  Base = (0,0,0)
  ClaimChildren = false
  Fit = 0
  FitJoin = 0
  FixShape = 1
  InnerFit = 0
  InnerFitJoin = 0
  InvalidShape = false
  NewSolid = false
  Placement = pos=(0,0,0) rot=(1,0,0;1.5708rad)
  Profile = -> Sketch197
  ReferenceAxis = -> Sketch197 [V_Axis]
  Refine = true
  Reversed = true
  Suppress = false
  TreeRank = 0
  ValidateShape = false
  _ProfileBasedVersion = 1
FEATURE [PartDesign::Fillet] Fillet047
  AddSubType = 0
  Base = -> Revolution001 [Edge2]
  BaseFeature = -> Revolution001
  FixShape = 1
  InvalidShape = false
  NewSolid = false
  Placement = pos=(0,0,0) rot=(1,0,0;1.5708rad)
  Radius = 7
  Refine = true
  SupportTransform = false
  Suppress = false
  TreeRank = 0
  UseAllEdges = false
  ValidateShape = false
FEATURE [Sketcher::SketchObject] Sketch198
  ArcFitTolerance = 0
  AttachmentOffset = pos=(0,0,25) rot=(0,0,1;0rad)
  AttachmentSupport = -> [XZ_Plane112]
  ExternalBSplineMaxDegree = 0
  ExternalBSplineTolerance = 0
  FixShape = 1
  FullyConstrained = false
  InternalTolerance = 1e-06
  InvalidShape = false
  MakeInternals = false
  MapMode = 5
  Placement = pos=(0,-25,-5.6e-15) rot=(1,0,0;1.5708rad)
  Support = -> [XZ_Plane112]
  TreeRank = 129
  ValidateShape = false
  sketch-geometry (2):
    g0: Circle CenterX=-16.1575 CenterY=33.1 CenterZ=0 NormalX=0 NormalY=0 NormalZ=1 AngleXU=0 Radius=4.03782
    g1: Circle CenterX=16.1575 CenterY=33.1 CenterZ=0 NormalX=0 NormalY=0 NormalZ=1 AngleXU=0 Radius=4.91935
  constraints (2):
    c: DistanceY(g0) = 33.1
    c: Symmetric(g1,g0,g-2)
FEATURE [PartDesign::Pocket] Pocket063
  AddSubType = 1
  AutoTaperInnerAngle = false
  BaseFeature = -> Fillet047
  CheckUpToFaceLimits = true
  ClaimChildren = false
  Direction = (1,1,1)
  Fit = 0
  FitJoin = 0
  FixShape = 1
  InnerFit = 0
  InnerFitJoin = 0
  InvalidShape = false
  Length = 5
  Length2 = 100
  Linearize = true
  NewSolid = false
  Placement = pos=(0,0,0) rot=(1,0,0;1.5708rad)
  Profile = -> Sketch198
  Refine = true
  Reversed = true
  Suppress = false
  TaperInnerAngle = 0
  TaperInnerAngleRev = 0
  TreeRank = 0
  Type = 1
  ValidateShape = false
  _ProfileBasedVersion = 1
  _Version = 1
FEATURE [PartDesign::Body] Body093  label="Head G2"
  AutoGroupSolids = false
  ClaimAllChildren = false
  ExportMode = 0
  FixShape = 1
  Group = -> [Binder,Sketch197,Revolution001,Fillet047,Sketch198,Pocket063]
  InvalidShape = false
  Origin = -> Origin007
  SingleSolid = true
  Tip = -> Pocket063
  TreeRank = 0
  ValidateShape = false
  _ExportChildren = -> [Binder,Revolution001,Fillet047,Pocket063]
  _GroupVersion = 1
FEATURE [Sketcher::SketchObject] Sketch199
  ArcFitTolerance = 0
  AttachmentSupport = -> [XY_Plane113]
  ExternalBSplineMaxDegree = 0
  ExternalBSplineTolerance = 0
  FixShape = 1
  FullyConstrained = true
  InternalTolerance = 1e-06
  InvalidShape = false
  MakeInternals = false
  MapMode = 5
  Support = -> [XY_Plane113]
  TreeRank = 136
  ValidateShape = false
  sketch-geometry (1):
    g0: Circle CenterX=0 CenterY=0 CenterZ=0 NormalX=0 NormalY=0 NormalZ=1 AngleXU=0 Radius=1000
  constraints (2):
    c: Coincident(g0,g-1)
    c: Diameter(g0) = 2000
FEATURE [PartDesign::Pad] Pad080
  AddSubType = 0
  AlongSketchNormal = false
  AutoTaperInnerAngle = false
  CheckUpToFaceLimits = true
  ClaimChildren = false
  Direction = (0,0,1)
  Fit = 0
  FitJoin = 0
  FixShape = 1
  InnerFit = 0
  InnerFitJoin = 0
  InvalidShape = false
  Length = 1
  Length2 = 100
  Linearize = true
  NewSolid = false
  Profile = -> Sketch199
  Refine = true
  Suppress = false
  TaperInnerAngle = 0
  TaperInnerAngleRev = 0
  TreeRank = 12
  Type = 0
  ValidateShape = false
  _ProfileBasedVersion = 1
FEATURE [PartDesign::Body] Body094  label="Field"
  AutoGroupSolids = false
  ClaimAllChildren = false
  ExportMode = 0
  FixShape = 1
  Group = -> [Sketch199,Pad080]
  InvalidShape = false
  Origin = -> Origin184
  Placement = pos=(0,0,32.5) rot=(0,0,1;0rad)
  SingleSolid = true
  Tip = -> Pad080
  TreeRank = 10
  ValidateShape = false
  _ExportChildren = -> [Pad080]
  _GroupVersion = 1
COMPONENT P15 — recipe-attached ("LD06", modeled in this document).
Construction recipe (the document's own serialized feature program — sketch geometry with constraints, then the solid features built on it; lengths are millimeters unless a unit is written):

FEATURE [Sketcher::SketchObject] Sketch189
  ArcFitTolerance = 0
  AttachmentSupport = -> [XY_Plane109]
  ExternalBSplineMaxDegree = 0
  ExternalBSplineTolerance = 0
  FixShape = 1
  FullyConstrained = true
  InternalTolerance = 1e-06
  InvalidShape = false
  MakeInternals = false
  MapMode = 5
  Support = -> [XY_Plane109]
  TreeRank = 58
  ValidateShape = false
  sketch-geometry (10):
    g0: ArcOfCircle CenterX=-14.1 CenterY=14.1 CenterZ=0 NormalX=0 NormalY=0 NormalZ=1 AngleXU=0 Radius=5.195 StartAngle=1.5708 EndAngle=3.14159
    g1: LineSegment StartX=-14.1 StartY=19.295 StartZ=0 EndX=14.1 EndY=19.295 EndZ=0
    g2: ArcOfCircle CenterX=14.1 CenterY=14.1 CenterZ=0 NormalX=0 NormalY=0 NormalZ=1 AngleXU=0 Radius=5.195 StartAngle=6.5809e-12 EndAngle=1.5708
    g3: LineSegment StartX=19.295 StartY=14.1 StartZ=0 EndX=19.295 EndY=-14.1 EndZ=0
    g4: ArcOfCircle CenterX=14.1 CenterY=-14.1 CenterZ=0 NormalX=0 NormalY=0 NormalZ=1 AngleXU=0 Radius=5.195 StartAngle=4.71239 EndAngle=6.28319
    g5: LineSegment StartX=14.1 StartY=-19.295 StartZ=0 EndX=-14.1 EndY=-19.295 EndZ=0
    g6: ArcOfCircle CenterX=-14.1 CenterY=-14.1 CenterZ=0 NormalX=0 NormalY=0 NormalZ=1 AngleXU=0 Radius=5.195 StartAngle=3.14159 EndAngle=4.71239
    g7: LineSegment StartX=-19.295 StartY=-14.1 StartZ=0 EndX=-19.295 EndY=14.1 EndZ=0
    g8: GeomPoint [constr] X=-19.295 Y=19.295 Z=0
    g9: GeomPoint [constr] X=19.295 Y=-19.295 Z=0
  constraints (23):
    c: Tangent(g0,g1) = 1.5708
    c: Tangent(g1,g2) = 1.5708
    c: Tangent(g2,g3) = 1.5708
    c: Tangent(g3,g4) = 1.5708
    c: Tangent(g4,g5) = 1.5708
    c: Tangent(g5,g6) = 1.5708
    c: Tangent(g6,g7) = 1.5708
    c: Tangent(g7,g0) = 1.5708
    c: Horizontal(g1)
    c: Horizontal(g5)
    c: Vertical(g3)
    c: Vertical(g7)
    c: Equal(g0,g2)
    c: Equal(g2,g4)
    c: Equal(g4,g6)
    c: PointOnObject(g8,g1)
    c: PointOnObject(g8,g7)
    c: PointOnObject(g9,g3)
    c: PointOnObject(g9,g5)
    c: Symmetric(g0,g4,g-1)
    c: Equal(g1,g3)
    c: DistanceY(g4,g1) = 38.59
    c: DistanceX(g0,g2) = 28.2
FEATURE [PartDesign::Pad] Pad077
  AddSubType = 0
  AlongSketchNormal = false
  AutoTaperInnerAngle = false
  CheckUpToFaceLimits = true
  ClaimChildren = false
  Direction = (0,0,1)
  Fit = 0
  FitJoin = 0
  FixShape = 1
  InnerFit = 0
  InnerFitJoin = 0
  InvalidShape = false
  Length = 20.7
  Length2 = 100
  Linearize = true
  NewSolid = false
  Profile = -> Sketch189
  Refine = true
  Suppress = false
  TaperAngle = -2
  TaperInnerAngle = 0
  TaperInnerAngleRev = 0
  TreeRank = 59
  Type = 0
  ValidateShape = false
  _ProfileBasedVersion = 1
FEATURE [Sketcher::SketchObject] Sketch190
  ArcFitTolerance = 0
  AttachmentSupport = -> [Pad077]
  ExternalBSplineMaxDegree = 0
  ExternalBSplineTolerance = 0
  FixShape = 1
  FullyConstrained = true
  InternalTolerance = 1e-06
  InvalidShape = false
  MakeInternals = false
  MapMode = 5
  Placement = pos=(0,0,20.7) rot=(0,0,1;0rad)
  Support = -> [Pad077]
  TreeRank = 60
  ValidateShape = false
  sketch-geometry (1):
    g0: Circle CenterX=0 CenterY=0 CenterZ=0 NormalX=0 NormalY=0 NormalZ=1 AngleXU=0 Radius=17.645
  constraints (2):
    c: Coincident(g0,g-1)
    c: Diameter(g0) = 35.29
FEATURE [PartDesign::Pad] Pad078
  AddSubType = 0
  AlongSketchNormal = false
  AutoTaperInnerAngle = false
  BaseFeature = -> Pad077
  CheckUpToFaceLimits = true
  ClaimChildren = false
  Direction = (0,0,1)
  Fit = 0
  FitJoin = 0
  FixShape = 1
  InnerFit = 0
  InnerFitJoin = 0
  InvalidShape = false
  Length = 12.8
  Length2 = 100
  Linearize = true
  NewSolid = false
  Profile = -> Sketch190
  Refine = true
  Suppress = false
  TaperAngle = -1.5
  TaperInnerAngle = 0
  TaperInnerAngleRev = 0
  TreeRank = 61
  Type = 0
  ValidateShape = false
  _ProfileBasedVersion = 1
FEATURE [Sketcher::SketchObject] Sketch191
  ArcFitTolerance = 0
  AttachmentOffset = pos=(0,0,17) rot=(0,0,1;0rad)
  AttachmentSupport = -> [XZ_Plane109]
  ExternalBSplineMaxDegree = 0
  ExternalBSplineTolerance = 0
  FixShape = 1
  FullyConstrained = true
  InternalTolerance = 1e-06
  InvalidShape = false
  MakeInternals = false
  MapMode = 5
  Placement = pos=(0,-17,-3.8e-15) rot=(1,0,0;1.5708rad)
  Support = -> [XZ_Plane109]
  TreeRank = 62
  ValidateShape = false
  sketch-geometry (5):
    g0: LineSegment StartX=-5 StartY=6.3 StartZ=0 EndX=-5 EndY=1.3 EndZ=0
    g1: LineSegment StartX=-5 StartY=1.3 StartZ=0 EndX=5 EndY=1.3 EndZ=0
    g2: LineSegment StartX=5 StartY=1.3 StartZ=0 EndX=5 EndY=6.3 EndZ=0
    g3: LineSegment StartX=5 StartY=6.3 StartZ=0 EndX=-5 EndY=6.3 EndZ=0
    g4: GeomPoint [constr] X=1.3758e-12 Y=3.8 Z=0
  constraints (13):
    c: Coincident(g0,g1)
    c: Coincident(g1,g2)
    c: Coincident(g2,g3)
    c: Coincident(g3,g0)
    c: Horizontal(g1)
    c: Horizontal(g3)
    c: Vertical(g0)
    c: Vertical(g2)
    c: Symmetric(g1,g0,g4)
    c: PointOnObject(g4,g-2)
    c: DistanceX(g3,g3) = 10
    c: DistanceY(g2,g2) = 5
    c: DistanceY(g-1,g4) = 3.8
FEATURE [PartDesign::Pocket] Pocket061
  AddSubType = 1
  AutoTaperInnerAngle = false
  BaseFeature = -> Pad078
  CheckUpToFaceLimits = true
  ClaimChildren = false
  Direction = (1,1,1)
  Fit = 0
  FitJoin = 0
  FixShape = 1
  InnerFit = 0
  InnerFitJoin = 0
  InvalidShape = false
  Length = 5
  Length2 = 100
  Linearize = true
  NewSolid = false
  Profile = -> Sketch191
  Refine = true
  Reversed = true
  Suppress = false
  TaperInnerAngle = 0
  TaperInnerAngleRev = 0
  TreeRank = 64
  Type = 1
  ValidateShape = false
  _ProfileBasedVersion = 1
  _Version = 1
FEATURE [Sketcher::SketchObject] Sketch192
  ArcFitTolerance = 0
  AttachmentSupport = -> [Pocket061]
  ExternalBSplineMaxDegree = 0
  ExternalBSplineTolerance = 0
  FixShape = 1
  FullyConstrained = false
  InternalTolerance = 1e-06
  InvalidShape = false
  MakeInternals = false
  MapMode = 5
  Placement = pos=(0,-17,0) rot=(1,0,0;1.5708rad)
  Support = -> [Pocket061]
  TreeRank = 65
  ValidateShape = false
  sketch-geometry (8):
    g0: Circle CenterX=-2.295 CenterY=3.8 CenterZ=0 NormalX=0 NormalY=0 NormalZ=1 AngleXU=0 Radius=0.765
    g1: Circle CenterX=-0.765 CenterY=3.8 CenterZ=0 NormalX=0 NormalY=0 NormalZ=1 AngleXU=0 Radius=0.765
    g2: Circle CenterX=0.765 CenterY=3.8 CenterZ=0 NormalX=0 NormalY=0 NormalZ=1 AngleXU=0 Radius=0.765
    g3: Circle CenterX=2.295 CenterY=3.8 CenterZ=0 NormalX=0 NormalY=0 NormalZ=1 AngleXU=0 Radius=0.765
    g4: LineSegment [constr] StartX=-2.295 StartY=3.8 StartZ=0 EndX=-0.765 EndY=3.8 EndZ=0
    g5: LineSegment [constr] StartX=-0.765 StartY=3.8 StartZ=0 EndX=0.765 EndY=3.8 EndZ=0
    g6: LineSegment [constr] StartX=0.765 StartY=3.8 StartZ=0 EndX=2.295 EndY=3.8 EndZ=0
    g7: GeomPoint [constr] X=1.8986e-12 Y=3.8 Z=0
  constraints (16):
    c: Horizontal(g3,g2)
    c: Symmetric(g1,g2,g-2)
    c: Symmetric(g0,g3,g-2)
    c: Coincident(g4,g0)
    c: Coincident(g4,g1)
    c: Coincident(g5,g1)
    c: Coincident(g5,g2)
    c: Coincident(g6,g2)
    c: Coincident(g6,g3)
    c: Equal(g6,g5)
    c: PointOnObject(g7,g5)
    c: Equal(g0,g1)
    c: Equal(g1,g2)
    c: Equal(g2,g3)
    c: Tangent(g3,g2)
    c: DistanceX(g4,g4) = 1.53
FEATURE [PartDesign::Pad] Pad079
  AddSubType = 0
  AlongSketchNormal = false
  AutoTaperInnerAngle = false
  BaseFeature = -> Pocket061
  CheckUpToFaceLimits = true
  ClaimChildren = false
  Direction = (0,-1,2e-16)
  Fit = 0
  FitJoin = 0
  FixShape = 1
  InnerFit = 0
  InnerFitJoin = 0
  InvalidShape = false
  Length = 10
  Length2 = 100
  Linearize = true
  NewSolid = false
  Profile = -> Sketch192
  Refine = true
  Suppress = false
  TaperInnerAngle = 0
  TaperInnerAngleRev = 0
  TreeRank = 66
  Type = 0
  ValidateShape = false
  _ProfileBasedVersion = 1
FEATURE [PartDesign::Fillet] Fillet045
  AddSubType = 0
  Base = -> Pad079 [Edge36]
  BaseFeature = -> Pad079
  FixShape = 1
  InvalidShape = false
  NewSolid = false
  Radius = 1
  Refine = true
  SupportTransform = false
  Suppress = false
  TreeRank = 67
  UseAllEdges = false
  ValidateShape = false
FEATURE [PartDesign::Fillet] Fillet046
  AddSubType = 0
  Base = -> Fillet045 [Edge13]
  BaseFeature = -> Fillet045
  FixShape = 1
  InvalidShape = false
  NewSolid = false
  Radius = 1
  Refine = true
  SupportTransform = false
  Suppress = false
  TreeRank = 68
  UseAllEdges = false
  ValidateShape = false
FEATURE [Sketcher::SketchObject] Sketch193
  ArcFitTolerance = 0
  AttachmentSupport = -> [Fillet046]
  ExternalBSplineMaxDegree = 0
  ExternalBSplineTolerance = 0
  FixShape = 1
  FullyConstrained = true
  InternalTolerance = 1e-06
  InvalidShape = false
  MakeInternals = false
  MapMode = 5
  Placement = pos=(0,0,33.5) rot=(0,0,1;0rad)
  Support = -> [Fillet046]
  TreeRank = 69
  ValidateShape = false
  sketch-geometry (3):
    g0: LineSegment StartX=13 StartY=-0.866025 StartZ=0 EndX=13 EndY=0.866025 EndZ=0
    g1: LineSegment StartX=13 StartY=0.866025 StartZ=0 EndX=14.5 EndY=-2.501e-11 EndZ=0
    g2: LineSegment StartX=14.5 StartY=-2.501e-11 StartZ=0 EndX=13 EndY=-0.866025 EndZ=0
  constraints (9):
    c: Vertical(g0)
    c: Coincident(g0,g1)
    c: PointOnObject(g1,g-1)
    c: Coincident(g1,g2)
    c: Coincident(g2,g0)
    c: Equal(g2,g1)
    c: Equal(g1,g0)
    c: DistanceX(g-1,g0) = 13
    c: DistanceX(g0,g1) = 1.5
FEATURE [PartDesign::Pocket] Pocket062
  AddSubType = 1
  AutoTaperInnerAngle = false
  BaseFeature = -> Fillet046
  CheckUpToFaceLimits = true
  ClaimChildren = false
  Direction = (1,1,1)
  Fit = 0
  FitJoin = 0
  FixShape = 1
  InnerFit = 0
  InnerFitJoin = 0
  InvalidShape = false
  Length = 1
  Length2 = 100
  Linearize = true
  NewSolid = false
  Profile = -> Sketch193
  Refine = true
  Suppress = false
  TaperInnerAngle = 0
  TaperInnerAngleRev = 0
  TreeRank = 70
  Type = 0
  ValidateShape = false
  _ProfileBasedVersion = 1
  _Version = 1
FEATURE [Sketcher::SketchObject] Sketch195
  ArcFitTolerance = 0
  AttachmentOffset = pos=(0,0,21.7) rot=(0,0,1;0rad)
  AttachmentSupport = -> [XY_Plane110]
  ExternalBSplineMaxDegree = 0
  ExternalBSplineTolerance = 0
  FixShape = 1
  FullyConstrained = true
  InternalTolerance = 1e-06
  InvalidShape = false
  MakeInternals = false
  MapMode = 5
  Placement = pos=(0,0,21.7) rot=(0,0,1;0rad)
  Support = -> [XY_Plane110]
  TreeRank = 81
  ValidateShape = false
  sketch-geometry (2):
    g0: Circle CenterX=0 CenterY=0 CenterZ=0 NormalX=0 NormalY=0 NormalZ=1 AngleXU=0 Radius=20
    g1: Circle CenterX=0 CenterY=0 CenterZ=0 NormalX=0 NormalY=0 NormalZ=1 AngleXU=0 Radius=500
  constraints (4):
    c: Coincident(g0,g-1)
    c: Coincident(g1,g0)
    c: Diameter(g1) = 1000
    c: Diameter(g0) = 40
FEATURE [PartDesign::Pad] Pad013
  AddSubType = 0
  AlongSketchNormal = false
  AutoTaperInnerAngle = false
  CheckUpToFaceLimits = true
  ClaimChildren = false
  Direction = (0,0,1)
  Fit = 0
  FitJoin = 0
  FixShape = 1
  InnerFit = 0
  InnerFitJoin = 0
  InvalidShape = false
  Length = 10
  Length2 = 100
  Linearize = true
  NewSolid = false
  Profile = -> Sketch195
  Refine = true
  Suppress = false
  TaperInnerAngle = 0
  TaperInnerAngleRev = 0
  TreeRank = 82
  Type = 0
  ValidateShape = false
  _ProfileBasedVersion = 1
FEATURE [PartDesign::Body] Body091  label="OpticalWindow"
  AutoGroupSolids = false
  ClaimAllChildren = false
  ExportMode = 0
  FixShape = 1
  Group = -> [Sketch195,Pad013]
  InvalidShape = false
  Origin = -> Origin182
  SingleSolid = true
  Tip = -> Pad013
  TreeRank = 80
  ValidateShape = false
  _ExportChildren = -> [Pad013]
  _GroupVersion = 1
FEATURE [PartDesign::Body] Body090  label="BaseLD06"
  AutoGroupSolids = false
  ClaimAllChildren = false
  ExportMode = 0
  FixShape = 1
  Group = -> [Sketch189,Pad077,Sketch190,Pad078,Sketch191,Pocket061,Sketch192,Pad079,Fillet045,Fillet046,Sketch193,Pocket062,Sketch194,Export,Export001,Pocket009,Pocket010]
  InvalidShape = false
  Origin = -> Origin181
  SingleSolid = true
  Tip = -> Pocket010
  TreeRank = 57
  ValidateShape = false
  _ExportChildren = -> [Pad077,Pad078,Pocket061,Pad079,Fillet045,Fillet046,Pocket062,Sketch194,Pocket009,Pocket010]
  _GroupVersion = 1
FEATURE [PartDesign::Pocket] Pocket010
  AddSubType = 1
  AutoTaperInnerAngle = false
  BaseFeature = -> Pocket009
  CheckUpToFaceLimits = true
  ClaimChildren = false
  Direction = (1,1,1)
  Fit = 0
  FitJoin = 0
  FixShape = 1
  InnerFit = 0
  InnerFitJoin = 0
  InvalidShape = false
  Length = 11.8
  Length2 = 100
  Linearize = true
  NewSolid = false
  Profile = -> Export
  Refine = true
  Suppress = false
  TaperInnerAngle = 0
  TaperInnerAngleRev = 0
  TreeRank = 170
  Type = 0
  ValidateShape = false
  _ProfileBasedVersion = 1
  _Version = 1
FEATURE [Sketcher::SketchObject] Sketch194
  ArcFitTolerance = 0
  AttachmentSupport = -> [XY_Plane109]
  Exports = -> [Export,Export001]
  ExternalBSplineMaxDegree = 0
  ExternalBSplineTolerance = 0
  FixShape = 1
  FullyConstrained = true
  InternalTolerance = 1e-06
  InvalidShape = false
  MakeInternals = false
  MapMode = 5
  Placement = pos=(0,0,0) rot=(0,1,0;3.14159rad)
  Support = -> [XY_Plane109]
  TreeRank = 84
  ValidateShape = false
  sketch-geometry (4):
    g0: Circle CenterX=-14.1 CenterY=14.1 CenterZ=0 NormalX=0 NormalY=0 NormalZ=1 AngleXU=0 Radius=2.4
    g1: Circle CenterX=14.1 CenterY=-14.1 CenterZ=0 NormalX=0 NormalY=0 NormalZ=1 AngleXU=0 Radius=2.4
    g2: Circle CenterX=-14.1 CenterY=14.1 CenterZ=0 NormalX=0 NormalY=0 NormalZ=1 AngleXU=0 Radius=1.225
    g3: Circle CenterX=14.1 CenterY=-14.1 CenterZ=0 NormalX=0 NormalY=0 NormalZ=1 AngleXU=0 Radius=1.225
  constraints (9):
    c: Symmetric(g0,g1,g-1)
    c: Equal(g0,g1)
    c: Diameter(g0) = 4.8
    c: DistanceX(g0,g-1) = 14.1
    c: DistanceY(g-1,g0) = 14.1
    c: Coincident(g2,g0)
    c: Coincident(g3,g1)
    c: Equal(g3,g2)
    c: Diameter(g3) = 2.45
FEATURE [Sketcher::SketchExport] Export
  Base = -> Sketch194
  BaseRefs = -> Sketch194 [edge1,edge2]
  FixShape = 1
  InvalidShape = false
  Placement = pos=(0,0,0) rot=(0,1,0;3.14159rad)
  Refs = ;g2.edge1 | ;g3.edge2
  SyncPlacement = true
  TreeRank = 85
  ValidateShape = false
FEATURE [Sketcher::SketchExport] Export001
  Base = -> Sketch194
  BaseRefs = -> Sketch194 [edge3,edge4]
  FixShape = 1
  InvalidShape = false
  Placement = pos=(0,0,0) rot=(0,1,0;3.14159rad)
  Refs = ;g4.edge3 | ;g5.edge4
  SyncPlacement = true
  TreeRank = 86
  ValidateShape = false
FEATURE [PartDesign::Pocket] Pocket009
  AddSubType = 1
  AutoTaperInnerAngle = false
  BaseFeature = -> Pocket062
  CheckUpToFaceLimits = true
  ClaimChildren = false
  Direction = (1,1,1)
  Fit = 0
  FitJoin = 0
  FixShape = 1
  InnerFit = 0
  InnerFitJoin = 0
  InvalidShape = false
  Length = 5
  Length2 = 100
  Linearize = true
  NewSolid = false
  Profile = -> Export001
  Refine = true
  Suppress = false
  TaperInnerAngle = 0
  TaperInnerAngleRev = 0
  TreeRank = 169
  Type = 1
  ValidateShape = false
  _ProfileBasedVersion = 1
  _Version = 1
COMPONENT P16 — recipe-attached ("MF128", modeled in this document).
Construction recipe (the document's own serialized feature program — sketch geometry with constraints, then the solid features built on it; lengths are millimeters unless a unit is written):

FEATURE [Sketcher::SketchObject] Sketch116
  ArcFitTolerance = 0
  AttachmentSupport = -> [XY_Plane062]
  ExternalBSplineMaxDegree = 0
  ExternalBSplineTolerance = 0
  FixShape = 1
  FullyConstrained = true
  InternalTolerance = 1e-06
  InvalidShape = false
  MakeInternals = false
  MapMode = 5
  Support = -> [XY_Plane062]
  TreeRank = 0
  ValidateShape = false
  sketch-geometry (10):
    g0: LineSegment StartX=-6.8 StartY=0 StartZ=0 EndX=-6.8 EndY=0.8 EndZ=0
    g1: LineSegment StartX=-6.8 StartY=0.8 StartZ=0 EndX=-5.4 EndY=0.8 EndZ=0
    g2: LineSegment StartX=-5.4 StartY=0.8 StartZ=0 EndX=-5.4 EndY=-2.7 EndZ=0
    g3: LineSegment StartX=-5.4 StartY=-2.7 StartZ=0 EndX=-6 EndY=-2.7 EndZ=0
    g4: LineSegment StartX=-6 StartY=-2.7 StartZ=0 EndX=-6 EndY=0 EndZ=0
    g5: LineSegment StartX=-6 StartY=0 StartZ=0 EndX=-6.8 EndY=0 EndZ=0
    g6: LineSegment StartX=-4.6 StartY=0.8 StartZ=0 EndX=-4 EndY=0.8 EndZ=0
    g7: LineSegment StartX=-4 StartY=0.8 StartZ=0 EndX=-4 EndY=-2.7 EndZ=0
    g8: LineSegment StartX=-4 StartY=-2.7 StartZ=0 EndX=-4.6 EndY=-2.7 EndZ=0
    g9: LineSegment StartX=-4.6 StartY=-2.7 StartZ=0 EndX=-4.6 EndY=0.8 EndZ=0
  constraints (30):
    c: Vertical(g0)
    c: Coincident(g0,g1)
    c: Horizontal(g1)
    c: Coincident(g1,g2)
    c: Vertical(g2)
    c: Coincident(g2,g3)
    c: Horizontal(g3)
    c: Coincident(g3,g4)
    c: Vertical(g4)
    c: Coincident(g4,g5)
    c: Coincident(g5,g0)
    c: Horizontal(g5)
    c: Coincident(g6,g7)
    c: Coincident(g7,g8)
    c: Coincident(g8,g9)
    c: Coincident(g9,g6)
    c: Horizontal(g6)
    c: Horizontal(g8)
    c: Vertical(g7)
    c: Vertical(g9)
    c: PointOnObject(g6,g1)
    c: PointOnObject(g4,g-1)
    c: DistanceY(g2,g2) = 3.5
    c: PointOnObject(g8,g3)
    c: DistanceX(g3) = -6
    c: DistanceX(g6) = -4
    c: Equal(g3,g6)
    c: DistanceX(g6,g6) = 0.6
    c: DistanceX(g0) = -6.8
    c: DistanceY(g0,g0) = 0.8
FEATURE [PartDesign::Revolution] Revolution005
  AddSubType = 0
  Angle = 360
  Axis = (0,1,0)
  Base = (0,0,0)
  ClaimChildren = false
  Fit = 0
  FitJoin = 0
  FixShape = 1
  InnerFit = 0
  InnerFitJoin = 0
  InvalidShape = false
  NewSolid = false
  Profile = -> Sketch116
  ReferenceAxis = -> Sketch116 [V_Axis]
  Refine = true
  Suppress = false
  TreeRank = 0
  ValidateShape = false
  _ProfileBasedVersion = 1
FEATURE [PartDesign::Body] Body052  label="CoreMF128"
  AutoGroupSolids = false
  ClaimAllChildren = false
  ExportMode = 0
  FixShape = 1
  Group = -> [Sketch116,Revolution005]
  InvalidShape = false
  Origin = -> Origin016
  Tip = -> Revolution005
  TreeRank = 0
  ValidateShape = false
  _ExportChildren = -> [Revolution005]
  _GroupVersion = 1
FEATURE [Sketcher::SketchObject] Sketch117
  ArcFitTolerance = 0
  AttachmentSupport = -> [XY_Plane063]
  ExternalBSplineMaxDegree = 0
  ExternalBSplineTolerance = 0
  FixShape = 1
  FullyConstrained = true
  InternalTolerance = 1e-06
  InvalidShape = false
  MakeInternals = false
  MapMode = 5
  Support = -> [XY_Plane063]
  TreeRank = 0
  ValidateShape = false
  sketch-geometry (4):
    g0: LineSegment StartX=-5.5 StartY=0.55 StartZ=0 EndX=-4.5 EndY=0.55 EndZ=0
    g1: LineSegment StartX=-4.5 StartY=0.55 StartZ=0 EndX=-4.5 EndY=-2.45 EndZ=0
    g2: LineSegment StartX=-4.5 StartY=-2.45 StartZ=0 EndX=-5.5 EndY=-2.45 EndZ=0
    g3: LineSegment StartX=-5.5 StartY=-2.45 StartZ=0 EndX=-5.5 EndY=0.55 EndZ=0
  constraints (12):
    c: Coincident(g0,g1)
    c: Coincident(g1,g2)
    c: Coincident(g2,g3)
    c: Coincident(g3,g0)
    c: Horizontal(g0)
    c: Horizontal(g2)
    c: Vertical(g1)
    c: Vertical(g3)
    c: DistanceY(g3,g3) = 3
    c: DistanceX(g0,g0) = 1
    c: DistanceX(g0,g-1) = 4.5
    c: DistanceY(g-1,g0) = 0.55
FEATURE [PartDesign::Revolution] Revolution006
  AddSubType = 0
  Angle = 360
  Axis = (0,1,0)
  Base = (0,0,0)
  ClaimChildren = false
  Fit = 0
  FitJoin = 0
  FixShape = 1
  InnerFit = 0
  InnerFitJoin = 0
  InvalidShape = false
  NewSolid = false
  Profile = -> Sketch117
  ReferenceAxis = -> Sketch117 [V_Axis]
  Refine = true
  Suppress = false
  TreeRank = 0
  ValidateShape = false
  _ProfileBasedVersion = 1
FEATURE [PartDesign::Body] Body053  label="SleeveMF128"
  AutoGroupSolids = false
  ClaimAllChildren = false
  ExportMode = 0
  FixShape = 1
  Group = -> [Sketch117,Revolution006]
  InvalidShape = false
  Origin = -> Origin080
  SingleSolid = true
  Tip = -> Revolution006
  TreeRank = 0
  ValidateShape = false
  _ExportChildren = -> [Revolution006]
  _GroupVersion = 1
COMPONENT P17 — recipe-attached ("MF83", modeled in this document).
Construction recipe (the document's own serialized feature program — sketch geometry with constraints, then the solid features built on it; lengths are millimeters unless a unit is written):

FEATURE [Sketcher::SketchObject] Sketch160
  ArcFitTolerance = 0
  AttachmentSupport = -> [XY_Plane091]
  ExternalBSplineMaxDegree = 0
  ExternalBSplineTolerance = 0
  FixShape = 1
  FullyConstrained = true
  InternalTolerance = 1e-06
  InvalidShape = false
  MakeInternals = false
  MapMode = 5
  Support = -> [XY_Plane091]
  TreeRank = 0
  ValidateShape = false
  sketch-geometry (10):
    g0: LineSegment StartX=-4.6 StartY=0 StartZ=0 EndX=-4.6 EndY=0.6 EndZ=0
    g1: LineSegment StartX=-4.6 StartY=0.6 StartZ=0 EndX=-3.4 EndY=0.6 EndZ=0
    g2: LineSegment StartX=-3.4 StartY=0.6 StartZ=0 EndX=-3.4 EndY=-2.4 EndZ=0
    g3: LineSegment StartX=-3.4 StartY=-2.4 StartZ=0 EndX=-4 EndY=-2.4 EndZ=0
    g4: LineSegment StartX=-4 StartY=-2.4 StartZ=0 EndX=-4 EndY=0 EndZ=0
    g5: LineSegment StartX=-4 StartY=0 StartZ=0 EndX=-4.6 EndY=0 EndZ=0
    g6: LineSegment StartX=-2.1 StartY=0.6 StartZ=0 EndX=-1.5 EndY=0.6 EndZ=0
    g7: LineSegment StartX=-1.5 StartY=0.6 StartZ=0 EndX=-1.5 EndY=-2.4 EndZ=0
    g8: LineSegment StartX=-1.5 StartY=-2.4 StartZ=0 EndX=-2.1 EndY=-2.4 EndZ=0
    g9: LineSegment StartX=-2.1 StartY=-2.4 StartZ=0 EndX=-2.1 EndY=0.6 EndZ=0
  constraints (30):
    c: Vertical(g0)
    c: Coincident(g0,g1)
    c: Horizontal(g1)
    c: Coincident(g1,g2)
    c: Vertical(g2)
    c: Coincident(g2,g3)
    c: Horizontal(g3)
    c: Coincident(g3,g4)
    c: Vertical(g4)
    c: Coincident(g4,g5)
    c: Coincident(g5,g0)
    c: Horizontal(g5)
    c: Coincident(g6,g7)
    c: Coincident(g7,g8)
    c: Coincident(g8,g9)
    c: Coincident(g9,g6)
    c: Horizontal(g6)
    c: Horizontal(g8)
    c: Vertical(g7)
    c: Vertical(g9)
    c: PointOnObject(g6,g1)
    c: PointOnObject(g4,g-1)
    c: DistanceY(g2,g2) = 3
    c: PointOnObject(g8,g3)
    c: DistanceX(g3) = -4
    c: DistanceX(g6) = -1.5
    c: Equal(g3,g6)
    c: DistanceX(g6,g6) = 0.6
    c: DistanceX(g0) = -4.6
    c: DistanceY(g0,g0) = 0.6
FEATURE [PartDesign::Revolution] Revolution010
  AddSubType = 0
  Angle = 360
  Axis = (0,1,0)
  Base = (0,0,0)
  ClaimChildren = false
  Fit = 0
  FitJoin = 0
  FixShape = 1
  InnerFit = 0
  InnerFitJoin = 0
  InvalidShape = false
  NewSolid = false
  Profile = -> Sketch160
  ReferenceAxis = -> Sketch160 [V_Axis]
  Refine = true
  Suppress = false
  TreeRank = 0
  ValidateShape = false
  _ProfileBasedVersion = 1
FEATURE [PartDesign::Body] Body074  label="CoreMF83"
  AutoGroupSolids = false
  ClaimAllChildren = false
  ExportMode = 0
  FixShape = 1
  Group = -> [Sketch160,Revolution010]
  InvalidShape = false
  Origin = -> Origin158
  Placement = pos=(0,2.84e-14,0) rot=(0,0,1;0rad)
  Tip = -> Revolution010
  TreeRank = 0
  ValidateShape = false
  _ExportChildren = -> [Revolution010]
  _GroupVersion = 1
FEATURE [Sketcher::SketchObject] Sketch161
  ArcFitTolerance = 0
  AttachmentSupport = -> [XY_Plane092]
  ExternalBSplineMaxDegree = 0
  ExternalBSplineTolerance = 0
  FixShape = 1
  FullyConstrained = true
  InternalTolerance = 1e-06
  InvalidShape = false
  MakeInternals = false
  MapMode = 5
  Support = -> [XY_Plane092]
  TreeRank = 0
  ValidateShape = false
  sketch-geometry (4):
    g0: LineSegment StartX=-3.4 StartY=0.5 StartZ=0 EndX=-2.1 EndY=0.5 EndZ=0
    g1: LineSegment StartX=-2.1 StartY=0.5 StartZ=0 EndX=-2.1 EndY=-2.3 EndZ=0
    g2: LineSegment StartX=-2.1 StartY=-2.3 StartZ=0 EndX=-3.4 EndY=-2.3 EndZ=0
    g3: LineSegment StartX=-3.4 StartY=-2.3 StartZ=0 EndX=-3.4 EndY=0.5 EndZ=0
  constraints (12):
    c: Coincident(g0,g1)
    c: Coincident(g1,g2)
    c: Coincident(g2,g3)
    c: Coincident(g3,g0)
    c: Horizontal(g0)
    c: Horizontal(g2)
    c: Vertical(g1)
    c: Vertical(g3)
    c: DistanceY(g3,g3) = 2.8
    c: DistanceX(g0,g0) = 1.3
    c: DistanceX(g0,g-1) = 2.1
    c: DistanceY(g-1,g0) = 0.5
FEATURE [PartDesign::Revolution] Revolution011
  AddSubType = 0
  Angle = 360
  Axis = (1e-16,1,-1e-16)
  Base = (0,0,0)
  ClaimChildren = false
  Fit = 0
  FitJoin = 0
  FixShape = 1
  InnerFit = 0
  InnerFitJoin = 0
  InvalidShape = false
  NewSolid = false
  Profile = -> Sketch161
  ReferenceAxis = -> Y_Axis092
  Refine = true
  Suppress = false
  TreeRank = 0
  ValidateShape = false
  _ProfileBasedVersion = 1
FEATURE [PartDesign::Body] Body075  label="SleeveMF83"
  AutoGroupSolids = false
  ClaimAllChildren = false
  ExportMode = 0
  FixShape = 1
  Group = -> [Sketch161,Revolution011]
  InvalidShape = false
  Origin = -> Origin159
  Placement = pos=(0,2.84e-14,0) rot=(0,0,1;0rad)
  SingleSolid = true
  Tip = -> Revolution011
  TreeRank = 0
  ValidateShape = false
  _ExportChildren = -> [Revolution011]
  _GroupVersion = 1
COMPONENT P18 — recipe-attached ("633ZZ", modeled in this document).
Construction recipe (the document's own serialized feature program — sketch geometry with constraints, then the solid features built on it; lengths are millimeters unless a unit is written):

FEATURE [Sketcher::SketchObject] Sketch169
  ArcFitTolerance = 0
  AttachmentSupport = -> [XZ_Plane100]
  ExternalBSplineMaxDegree = 0
  ExternalBSplineTolerance = 0
  FixShape = 1
  FullyConstrained = true
  InternalTolerance = 1e-06
  InvalidShape = false
  MakeInternals = false
  MapMode = 5
  Placement = pos=(0,0,0) rot=(1,0,0;1.5708rad)
  Support = -> [XZ_Plane100]
  TreeRank = 0
  ValidateShape = false
  sketch-geometry (12):
    g0: LineSegment StartX=-5.5 StartY=1.2718e-12 StartZ=0 EndX=-6.5 EndY=1.052e-12 EndZ=0
    g1: LineSegment StartX=-6.5 StartY=1.052e-12 StartZ=0 EndX=-6.5 EndY=5 EndZ=0
    g2: LineSegment StartX=-6.5 StartY=5 StartZ=0 EndX=-5.5 EndY=5 EndZ=0
    g3: LineSegment StartX=-5.5 StartY=5 StartZ=0 EndX=-5.5 EndY=4.6 EndZ=0
    g4: LineSegment StartX=-5.5 StartY=4.6 StartZ=0 EndX=-2.5 EndY=4.6 EndZ=0
    g5: LineSegment StartX=-2.5 StartY=4.6 StartZ=0 EndX=-2.5 EndY=5 EndZ=0
    g6: LineSegment StartX=-2.5 StartY=5 StartZ=0 EndX=-1.5 EndY=5 EndZ=0
    g7: LineSegment StartX=-1.5 StartY=5 StartZ=0 EndX=-1.5 EndY=0 EndZ=0
    g8: LineSegment StartX=-1.5 StartY=0 StartZ=0 EndX=-2.5 EndY=0 EndZ=0
    g9: LineSegment StartX=-2.5 StartY=0 StartZ=0 EndX=-2.5 EndY=0.4 EndZ=0
    g10: LineSegment StartX=-2.5 StartY=0.4 StartZ=0 EndX=-5.5 EndY=0.4 EndZ=0
    g11: LineSegment StartX=-5.5 StartY=0.4 StartZ=0 EndX=-5.5 EndY=1.2718e-12 EndZ=0
  constraints (36):
    c: PointOnObject(g0,g-1)
    c: PointOnObject(g0,g-1)
    c: Coincident(g0,g1)
    c: Vertical(g1)
    c: Coincident(g1,g2)
    c: Horizontal(g2)
    c: Coincident(g2,g3)
    c: Vertical(g3)
    c: Coincident(g3,g4)
    c: Horizontal(g4)
    c: Coincident(g4,g5)
    c: Vertical(g5)
    c: Coincident(g5,g6)
    c: Horizontal(g6)
    c: Coincident(g6,g7)
    c: PointOnObject(g7,g-1)
    c: Vertical(g7)
    c: Coincident(g7,g8)
    c: PointOnObject(g8,g-1)
    c: Coincident(g8,g9)
    c: Vertical(g9)
    c: Coincident(g9,g10)
    c: Horizontal(g10)
    c: Coincident(g10,g11)
    c: Coincident(g11,g0)
    c: Vertical(g11)
    c: DistanceX(g7) = -1.5
    c: DistanceX(g0) = -6.5
    c: Equal(g8,g0)
    c: Equal(g2,g6)
    c: Equal(g4,g10)
    c: Equal(g3,g11)
    c: DistanceY(g3,g3) = 0.4
    c: DistanceX(g8,g8) = 1
    c: DistanceY(g1,g1) = 5
    c: PointOnObject(g2,g6)
FEATURE [PartDesign::Revolution] Revolution012
  AddSubType = 0
  Angle = 360
  Axis = (0,-2e-16,1)
  Base = (0,0,0)
  ClaimChildren = false
  Fit = 0
  FitJoin = 0
  FixShape = 1
  InnerFit = 0
  InnerFitJoin = 0
  InvalidShape = false
  NewSolid = false
  Placement = pos=(0,0,0) rot=(1,0,0;1.5708rad)
  Profile = -> Sketch169
  ReferenceAxis = -> Sketch169 [V_Axis]
  Refine = true
  Suppress = false
  TreeRank = 0
  ValidateShape = false
  _ProfileBasedVersion = 0
FEATURE [PartDesign::Body] Body080  label="CoreMR149"
  AutoGroupSolids = false
  ClaimAllChildren = false
  ExportMode = 0
  FixShape = 1
  Group = -> [Sketch169,Revolution012]
  InvalidShape = false
  Origin = -> Origin166
  SingleSolid = true
  Tip = -> Revolution012
  TreeRank = 94
  ValidateShape = false
  _ExportChildren = -> [Revolution012]
  _GroupVersion = 1
FEATURE [Sketcher::SketchObject] Sketch170
  ArcFitTolerance = 0
  AttachmentSupport = -> [XZ_Plane101]
  ExternalBSplineMaxDegree = 0
  ExternalBSplineTolerance = 0
  FixShape = 1
  FullyConstrained = true
  InternalTolerance = 1e-06
  InvalidShape = false
  MakeInternals = false
  MapMode = 5
  Placement = pos=(0,0,0) rot=(1,0,0;1.5708rad)
  Support = -> [XZ_Plane101]
  TreeRank = 0
  ValidateShape = false
  sketch-geometry (4):
    g0: LineSegment StartX=-5.5 StartY=5 StartZ=0 EndX=-2.5 EndY=5 EndZ=0
    g1: LineSegment StartX=-2.5 StartY=5 StartZ=0 EndX=-2.5 EndY=0 EndZ=0
    g2: LineSegment StartX=-2.5 StartY=3e-16 StartZ=0 EndX=-5.5 EndY=3e-16 EndZ=0
    g3: LineSegment StartX=-5.5 StartY=3e-16 StartZ=0 EndX=-5.5 EndY=5 EndZ=0
  constraints (12):
    c: Coincident(g0,g1)
    c: Coincident(g1,g2)
    c: Coincident(g2,g3)
    c: Coincident(g3,g0)
    c: Horizontal(g0)
    c: Horizontal(g2)
    c: Vertical(g1)
    c: Vertical(g3)
    c: PointOnObject(g1,g-1)
    c: DistanceY(g3,g3) = 5
    c: DistanceX(g1) = -2.5
    c: DistanceX(g2) = -5.5
FEATURE [PartDesign::Revolution] Revolution013
  AddSubType = 0
  Angle = 360
  Axis = (0,-2e-16,1)
  Base = (0,0,0)
  ClaimChildren = false
  Fit = 0
  FitJoin = 0
  FixShape = 1
  InnerFit = 0
  InnerFitJoin = 0
  InvalidShape = false
  NewSolid = false
  Placement = pos=(0,0,0) rot=(1,0,0;1.5708rad)
  Profile = -> Sketch170
  ReferenceAxis = -> Sketch170 [V_Axis]
  Refine = true
  Suppress = false
  TreeRank = 0
  ValidateShape = false
  _ProfileBasedVersion = 0
FEATURE [PartDesign::Body] Body081  label="Sleeve001"
  AutoGroupSolids = false
  ClaimAllChildren = false
  ExportMode = 0
  FixShape = 1
  Group = -> [Sketch170,Revolution013]
  InvalidShape = false
  Origin = -> Origin167
  SingleSolid = true
  Tip = -> Revolution013
  TreeRank = 95
  ValidateShape = false
  _ExportChildren = -> [Revolution013]
  _GroupVersion = 1
